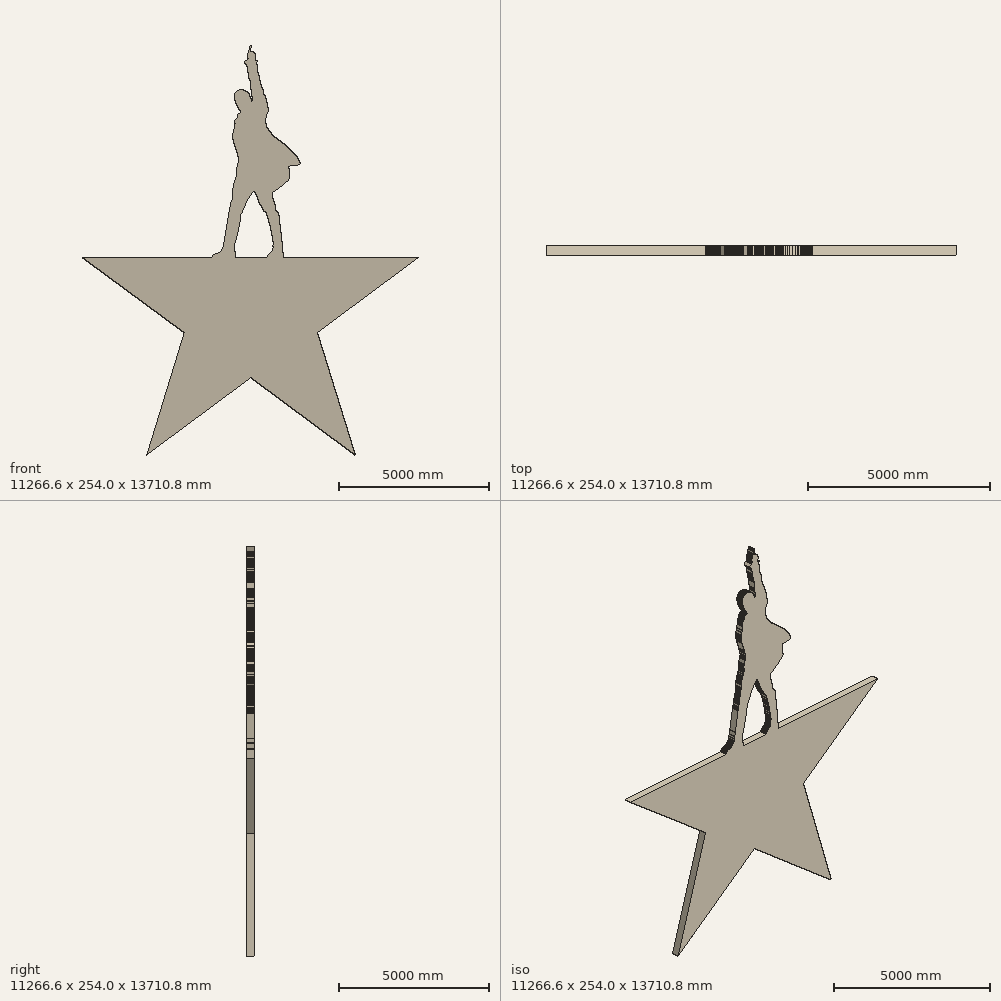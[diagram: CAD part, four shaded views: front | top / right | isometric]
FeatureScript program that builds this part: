
annotation { "Feature Type Name" : "Feature", "Feature Type Description" : "" }
export const myFeature = defineFeature(function(context is Context, id is Id, definition is map)
    precondition{}
    {
        {
            var Q0;
            Q0=qCreatedBy(makeId("Front.planeOp"),FACE);
            var sketch = newSketch(context, id + "F0", { "sketchPlane" : qUnion([Q0])});
            skLineSegment(sketch, "E0", {"start": v(-2213.01, -2754.08) * mm, "end": v(-3464.1, -6842.16) * mm});
            skLineSegment(sketch, "E1", {"start": v(-3464.1, -6842.16) * mm, "end": v(18.56, -4260.23) * mm});
            skLineSegment(sketch, "E2", {"start": v(18.56, -4260.23) * mm, "end": v(3513.04, -6855.37) * mm});
            skLineSegment(sketch, "E3", {"start": v(3513.04, -6855.37) * mm, "end": v(2240.88, -2755) * mm});
            skLineSegment(sketch, "E4", {"start": v(2240.88, -2755) * mm, "end": v(5633.28, -233.2) * mm});
            skLineSegment(sketch, "E5", {"start": v(5633.28, -233.2) * mm, "end": v(1116.7, -233.2) * mm});
            skLineSegment(sketch, "E6", {"start": v(1116.7, -233.2) * mm, "end": v(1111.2, -233.12) * mm});
            skLineSegment(sketch, "E7", {"start": v(1111.2, -233.12) * mm, "end": v(1117, -229) * mm});
            skLineSegment(sketch, "E8", {"start": v(1117, -229) * mm, "end": v(1065.8, 66.4) * mm});
            skLineSegment(sketch, "E9", {"start": v(1065.8, 66.4) * mm, "end": v(1064.67, 70.05) * mm});
            skLineSegment(sketch, "E10", {"start": v(1064.67, 70.05) * mm, "end": v(1064.67, 73.83) * mm});
            skLineSegment(sketch, "E11", {"start": v(1064.67, 73.83) * mm, "end": v(1064.87, 89.05) * mm});
            skLineSegment(sketch, "E12", {"start": v(1064.87, 89.05) * mm, "end": v(1057.1, 259.32) * mm});
            skLineSegment(sketch, "E13", {"start": v(1057.1, 259.32) * mm, "end": v(1054.52, 304.4) * mm});
            skLineSegment(sketch, "E14", {"start": v(1054.52, 304.4) * mm, "end": v(1051.17, 338.35) * mm});
            skLineSegment(sketch, "E15", {"start": v(1051.17, 338.35) * mm, "end": v(1041.6, 435.3) * mm});
            skLineSegment(sketch, "E16", {"start": v(1041.6, 435.3) * mm, "end": v(939.6, 1264.76) * mm});
            skLineSegment(sketch, "E17", {"start": v(939.6, 1264.76) * mm, "end": v(938.4, 1268.61) * mm});
            skLineSegment(sketch, "E18", {"start": v(938.4, 1268.61) * mm, "end": v(935.27, 1273.03) * mm});
            skLineSegment(sketch, "E19", {"start": v(935.27, 1273.03) * mm, "end": v(931.23, 1277.44) * mm});
            skLineSegment(sketch, "E20", {"start": v(931.23, 1277.44) * mm, "end": v(926.86, 1281.5) * mm});
            skLineSegment(sketch, "E21", {"start": v(926.86, 1281.5) * mm, "end": v(921.55, 1284.85) * mm});
            skLineSegment(sketch, "E22", {"start": v(921.55, 1284.85) * mm, "end": v(916.4, 1287.12) * mm});
            skLineSegment(sketch, "E23", {"start": v(916.4, 1287.12) * mm, "end": v(911.88, 1288.5) * mm});
            skLineSegment(sketch, "E24", {"start": v(911.88, 1288.5) * mm, "end": v(900.62, 1290.1) * mm});
            skLineSegment(sketch, "E25", {"start": v(900.62, 1290.1) * mm, "end": v(890.87, 1292.59) * mm});
            skLineSegment(sketch, "E26", {"start": v(890.87, 1292.59) * mm, "end": v(882.3, 1295.94) * mm});
            skLineSegment(sketch, "E27", {"start": v(882.3, 1295.94) * mm, "end": v(874.94, 1300.12) * mm});
            skLineSegment(sketch, "E28", {"start": v(874.94, 1300.12) * mm, "end": v(868.75, 1305.14) * mm});
            skLineSegment(sketch, "E29", {"start": v(868.75, 1305.14) * mm, "end": v(863.55, 1310.99) * mm});
            skLineSegment(sketch, "E30", {"start": v(863.55, 1310.99) * mm, "end": v(859.3, 1317.69) * mm});
            skLineSegment(sketch, "E31", {"start": v(859.3, 1317.69) * mm, "end": v(855.94, 1325.24) * mm});
            skLineSegment(sketch, "E32", {"start": v(855.94, 1325.24) * mm, "end": v(853.36, 1333.55) * mm});
            skLineSegment(sketch, "E33", {"start": v(853.36, 1333.55) * mm, "end": v(851.43, 1342.72) * mm});
            skLineSegment(sketch, "E34", {"start": v(851.43, 1342.72) * mm, "end": v(850.3, 1352.77) * mm});
            skLineSegment(sketch, "E35", {"start": v(850.3, 1352.77) * mm, "end": v(849.68, 1363.6) * mm});
            skLineSegment(sketch, "E36", {"start": v(849.68, 1363.6) * mm, "end": v(849.45, 1384.7) * mm});
            skLineSegment(sketch, "E37", {"start": v(849.45, 1384.7) * mm, "end": v(849.02, 1394.13) * mm});
            skLineSegment(sketch, "E38", {"start": v(849.02, 1394.13) * mm, "end": v(848.26, 1403.63) * mm});
            skLineSegment(sketch, "E39", {"start": v(848.26, 1403.63) * mm, "end": v(847.23, 1413.05) * mm});
            skLineSegment(sketch, "E40", {"start": v(847.23, 1413.05) * mm, "end": v(845.94, 1422.53) * mm});
            skLineSegment(sketch, "E41", {"start": v(845.94, 1422.53) * mm, "end": v(844.43, 1431.96) * mm});
            skLineSegment(sketch, "E42", {"start": v(844.43, 1431.96) * mm, "end": v(842.7, 1441.43) * mm});
            skLineSegment(sketch, "E43", {"start": v(842.7, 1441.43) * mm, "end": v(838.7, 1460.35) * mm});
            skLineSegment(sketch, "E44", {"start": v(838.7, 1460.35) * mm, "end": v(817.27, 1545) * mm});
            skLineSegment(sketch, "E45", {"start": v(817.27, 1545) * mm, "end": v(815.39, 1551.49) * mm});
            skLineSegment(sketch, "E46", {"start": v(815.39, 1551.49) * mm, "end": v(813.06, 1557.84) * mm});
            skLineSegment(sketch, "E47", {"start": v(813.06, 1557.84) * mm, "end": v(810.47, 1564.1) * mm});
            skLineSegment(sketch, "E48", {"start": v(810.47, 1564.1) * mm, "end": v(807.61, 1570.32) * mm});
            skLineSegment(sketch, "E49", {"start": v(807.61, 1570.32) * mm, "end": v(798.46, 1588.82) * mm});
            skLineSegment(sketch, "E50", {"start": v(798.46, 1588.82) * mm, "end": v(795.57, 1595.02) * mm});
            skLineSegment(sketch, "E51", {"start": v(795.57, 1595.02) * mm, "end": v(792.9, 1601.22) * mm});
            skLineSegment(sketch, "E52", {"start": v(792.9, 1601.22) * mm, "end": v(790.59, 1607.5) * mm});
            skLineSegment(sketch, "E53", {"start": v(790.59, 1607.5) * mm, "end": v(788.7, 1613.88) * mm});
            skLineSegment(sketch, "E54", {"start": v(788.7, 1613.88) * mm, "end": v(787.3, 1620.31) * mm});
            skLineSegment(sketch, "E55", {"start": v(787.3, 1620.31) * mm, "end": v(782.41, 1648.48) * mm});
            skLineSegment(sketch, "E56", {"start": v(782.41, 1648.48) * mm, "end": v(778.7, 1666.96) * mm});
            skLineSegment(sketch, "E57", {"start": v(778.7, 1666.96) * mm, "end": v(774.5, 1685.33) * mm});
            skLineSegment(sketch, "E58", {"start": v(774.5, 1685.33) * mm, "end": v(772.23, 1694.38) * mm});
            skLineSegment(sketch, "E59", {"start": v(772.23, 1694.38) * mm, "end": v(769.74, 1703.45) * mm});
            skLineSegment(sketch, "E60", {"start": v(769.74, 1703.45) * mm, "end": v(767.06, 1712.45) * mm});
            skLineSegment(sketch, "E61", {"start": v(767.06, 1712.45) * mm, "end": v(764.1, 1721.4) * mm});
            skLineSegment(sketch, "E62", {"start": v(764.1, 1721.4) * mm, "end": v(760.91, 1730.33) * mm});
            skLineSegment(sketch, "E63", {"start": v(760.91, 1730.33) * mm, "end": v(757.44, 1739.18) * mm});
            skLineSegment(sketch, "E64", {"start": v(757.44, 1739.18) * mm, "end": v(753.71, 1748.1) * mm});
            skLineSegment(sketch, "E65", {"start": v(753.71, 1748.1) * mm, "end": v(749.62, 1756.94) * mm});
            skLineSegment(sketch, "E66", {"start": v(749.62, 1756.94) * mm, "end": v(745.2, 1765.77) * mm});
            skLineSegment(sketch, "E67", {"start": v(745.2, 1765.77) * mm, "end": v(740.43, 1774.57) * mm});
            skLineSegment(sketch, "E68", {"start": v(740.43, 1774.57) * mm, "end": v(736.92, 1781.4) * mm});
            skLineSegment(sketch, "E69", {"start": v(736.92, 1781.4) * mm, "end": v(733.92, 1788.58) * mm});
            skLineSegment(sketch, "E70", {"start": v(733.92, 1788.58) * mm, "end": v(731.4, 1796.02) * mm});
            skLineSegment(sketch, "E71", {"start": v(731.4, 1796.02) * mm, "end": v(729.35, 1803.69) * mm});
            skLineSegment(sketch, "E72", {"start": v(729.35, 1803.69) * mm, "end": v(727.64, 1811.55) * mm});
            skLineSegment(sketch, "E73", {"start": v(727.64, 1811.55) * mm, "end": v(726.26, 1819.64) * mm});
            skLineSegment(sketch, "E74", {"start": v(726.26, 1819.64) * mm, "end": v(725.16, 1827.86) * mm});
            skLineSegment(sketch, "E75", {"start": v(725.16, 1827.86) * mm, "end": v(724.32, 1836.2) * mm});
            skLineSegment(sketch, "E76", {"start": v(724.32, 1836.2) * mm, "end": v(723.7, 1844.65) * mm});
            skLineSegment(sketch, "E77", {"start": v(723.7, 1844.65) * mm, "end": v(721.68, 1887.31) * mm});
            skLineSegment(sketch, "E78", {"start": v(721.68, 1887.31) * mm, "end": v(720.62, 1903.98) * mm});
            skLineSegment(sketch, "E79", {"start": v(720.62, 1903.98) * mm, "end": v(721.15, 1907.55) * mm});
            skLineSegment(sketch, "E80", {"start": v(721.15, 1907.55) * mm, "end": v(723.06, 1911.39) * mm});
            skLineSegment(sketch, "E81", {"start": v(723.06, 1911.39) * mm, "end": v(726.07, 1915.34) * mm});
            skLineSegment(sketch, "E82", {"start": v(726.07, 1915.34) * mm, "end": v(729.83, 1919.26) * mm});
            skLineSegment(sketch, "E83", {"start": v(729.83, 1919.26) * mm, "end": v(734.03, 1923) * mm});
            skLineSegment(sketch, "E84", {"start": v(734.03, 1923) * mm, "end": v(738.38, 1926.42) * mm});
            skLineSegment(sketch, "E85", {"start": v(738.38, 1926.42) * mm, "end": v(742.53, 1929.36) * mm});
            skLineSegment(sketch, "E86", {"start": v(742.53, 1929.36) * mm, "end": v(818.36, 1978.85) * mm});
            skLineSegment(sketch, "E87", {"start": v(818.36, 1978.85) * mm, "end": v(875.1, 2016.17) * mm});
            skLineSegment(sketch, "E88", {"start": v(875.1, 2016.17) * mm, "end": v(903, 2035.42) * mm});
            skLineSegment(sketch, "E89", {"start": v(903, 2035.42) * mm, "end": v(910.4, 2040.9) * mm});
            skLineSegment(sketch, "E90", {"start": v(910.4, 2040.9) * mm, "end": v(917.61, 2046.72) * mm});
            skLineSegment(sketch, "E91", {"start": v(917.61, 2046.72) * mm, "end": v(924.7, 2052.77) * mm});
            skLineSegment(sketch, "E92", {"start": v(924.7, 2052.77) * mm, "end": v(959.14, 2084.25) * mm});
            skLineSegment(sketch, "E93", {"start": v(959.14, 2084.25) * mm, "end": v(966.12, 2090.3) * mm});
            skLineSegment(sketch, "E94", {"start": v(966.12, 2090.3) * mm, "end": v(973.22, 2096.12) * mm});
            skLineSegment(sketch, "E95", {"start": v(973.22, 2096.12) * mm, "end": v(980.46, 2101.63) * mm});
            skLineSegment(sketch, "E96", {"start": v(980.46, 2101.63) * mm, "end": v(987.9, 2106.74) * mm});
            skLineSegment(sketch, "E97", {"start": v(987.9, 2106.74) * mm, "end": v(995.56, 2111.43) * mm});
            skLineSegment(sketch, "E98", {"start": v(995.56, 2111.43) * mm, "end": v(1017.24, 2122.53) * mm});
            skLineSegment(sketch, "E99", {"start": v(1017.24, 2122.53) * mm, "end": v(1030.63, 2130) * mm});
            skLineSegment(sketch, "E100", {"start": v(1030.63, 2130) * mm, "end": v(1043.62, 2137.91) * mm});
            skLineSegment(sketch, "E101", {"start": v(1043.62, 2137.91) * mm, "end": v(1056.26, 2146.22) * mm});
            skLineSegment(sketch, "E102", {"start": v(1056.26, 2146.22) * mm, "end": v(1068.54, 2154.93) * mm});
            skLineSegment(sketch, "E103", {"start": v(1068.54, 2154.93) * mm, "end": v(1080.56, 2163.94) * mm});
            skLineSegment(sketch, "E104", {"start": v(1080.56, 2163.94) * mm, "end": v(1092.31, 2173.26) * mm});
            skLineSegment(sketch, "E105", {"start": v(1092.31, 2173.26) * mm, "end": v(1103.82, 2182.85) * mm});
            skLineSegment(sketch, "E106", {"start": v(1103.82, 2182.85) * mm, "end": v(1126.3, 2202.66) * mm});
            skLineSegment(sketch, "E107", {"start": v(1126.3, 2202.66) * mm, "end": v(1202.34, 2274.96) * mm});
            skLineSegment(sketch, "E108", {"start": v(1202.34, 2274.96) * mm, "end": v(1224.34, 2295.26) * mm});
            skLineSegment(sketch, "E109", {"start": v(1224.34, 2295.26) * mm, "end": v(1255.09, 2321.92) * mm});
            skLineSegment(sketch, "E110", {"start": v(1255.09, 2321.92) * mm, "end": v(1262.74, 2329.19) * mm});
            skLineSegment(sketch, "E111", {"start": v(1262.74, 2329.19) * mm, "end": v(1269.9, 2336.66) * mm});
            skLineSegment(sketch, "E112", {"start": v(1269.9, 2336.66) * mm, "end": v(1276.58, 2344.37) * mm});
            skLineSegment(sketch, "E113", {"start": v(1276.58, 2344.37) * mm, "end": v(1282.73, 2352.3) * mm});
            skLineSegment(sketch, "E114", {"start": v(1282.73, 2352.3) * mm, "end": v(1288.32, 2360.47) * mm});
            skLineSegment(sketch, "E115", {"start": v(1288.32, 2360.47) * mm, "end": v(1293.36, 2368.9) * mm});
            skLineSegment(sketch, "E116", {"start": v(1293.36, 2368.9) * mm, "end": v(1297.81, 2377.58) * mm});
            skLineSegment(sketch, "E117", {"start": v(1297.81, 2377.58) * mm, "end": v(1301.66, 2386.5) * mm});
            skLineSegment(sketch, "E118", {"start": v(1301.66, 2386.5) * mm, "end": v(1304.88, 2395.7) * mm});
            skLineSegment(sketch, "E119", {"start": v(1304.88, 2395.7) * mm, "end": v(1307.45, 2405.18) * mm});
            skLineSegment(sketch, "E120", {"start": v(1307.45, 2405.18) * mm, "end": v(1309.37, 2414.94) * mm});
            skLineSegment(sketch, "E121", {"start": v(1309.37, 2414.94) * mm, "end": v(1310.6, 2425) * mm});
            skLineSegment(sketch, "E122", {"start": v(1310.6, 2425) * mm, "end": v(1311.13, 2435.34) * mm});
            skLineSegment(sketch, "E123", {"start": v(1311.13, 2435.34) * mm, "end": v(1310.94, 2445.99) * mm});
            skLineSegment(sketch, "E124", {"start": v(1310.94, 2445.99) * mm, "end": v(1310, 2456.93) * mm});
            skLineSegment(sketch, "E125", {"start": v(1310, 2456.93) * mm, "end": v(1308.3, 2468.22) * mm});
            skLineSegment(sketch, "E126", {"start": v(1308.3, 2468.22) * mm, "end": v(1307.11, 2475.3) * mm});
            skLineSegment(sketch, "E127", {"start": v(1307.11, 2475.3) * mm, "end": v(1306.1, 2482.4) * mm});
            skLineSegment(sketch, "E128", {"start": v(1306.1, 2482.4) * mm, "end": v(1305.21, 2489.53) * mm});
            skLineSegment(sketch, "E129", {"start": v(1305.21, 2489.53) * mm, "end": v(1303.86, 2503.87) * mm});
            skLineSegment(sketch, "E130", {"start": v(1303.86, 2503.87) * mm, "end": v(1299.82, 2572.18) * mm});
            skLineSegment(sketch, "E131", {"start": v(1299.82, 2572.18) * mm, "end": v(1296.68, 2668.61) * mm});
            skLineSegment(sketch, "E132", {"start": v(1296.68, 2668.61) * mm, "end": v(1295.55, 2689.96) * mm});
            skLineSegment(sketch, "E133", {"start": v(1295.55, 2689.96) * mm, "end": v(1293.87, 2711.15) * mm});
            skLineSegment(sketch, "E134", {"start": v(1293.87, 2711.15) * mm, "end": v(1292.76, 2721.68) * mm});
            skLineSegment(sketch, "E135", {"start": v(1292.76, 2721.68) * mm, "end": v(1291.43, 2732.15) * mm});
            skLineSegment(sketch, "E136", {"start": v(1291.43, 2732.15) * mm, "end": v(1289.87, 2742.56) * mm});
            skLineSegment(sketch, "E137", {"start": v(1289.87, 2742.56) * mm, "end": v(1288.05, 2752.9) * mm});
            skLineSegment(sketch, "E138", {"start": v(1288.05, 2752.9) * mm, "end": v(1285.94, 2763.17) * mm});
            skLineSegment(sketch, "E139", {"start": v(1285.94, 2763.17) * mm, "end": v(1281.15, 2783.65) * mm});
            skLineSegment(sketch, "E140", {"start": v(1281.15, 2783.65) * mm, "end": v(1279.68, 2792.43) * mm});
            skLineSegment(sketch, "E141", {"start": v(1279.68, 2792.43) * mm, "end": v(1279.04, 2799.8) * mm});
            skLineSegment(sketch, "E142", {"start": v(1279.04, 2799.8) * mm, "end": v(1279.25, 2805.94) * mm});
            skLineSegment(sketch, "E143", {"start": v(1279.25, 2805.94) * mm, "end": v(1280.3, 2810.94) * mm});
            skLineSegment(sketch, "E144", {"start": v(1280.3, 2810.94) * mm, "end": v(1282.19, 2814.92) * mm});
            skLineSegment(sketch, "E145", {"start": v(1282.19, 2814.92) * mm, "end": v(1284.86, 2818.02) * mm});
            skLineSegment(sketch, "E146", {"start": v(1284.86, 2818.02) * mm, "end": v(1288.31, 2820.36) * mm});
            skLineSegment(sketch, "E147", {"start": v(1288.31, 2820.36) * mm, "end": v(1292.53, 2822.09) * mm});
            skLineSegment(sketch, "E148", {"start": v(1292.53, 2822.09) * mm, "end": v(1297.5, 2823.32) * mm});
            skLineSegment(sketch, "E149", {"start": v(1297.5, 2823.32) * mm, "end": v(1303.18, 2824.17) * mm});
            skLineSegment(sketch, "E150", {"start": v(1303.18, 2824.17) * mm, "end": v(1309.6, 2824.77) * mm});
            skLineSegment(sketch, "E151", {"start": v(1309.6, 2824.77) * mm, "end": v(1337.24, 2826.57) * mm});
            skLineSegment(sketch, "E152", {"start": v(1337.24, 2826.57) * mm, "end": v(1401.12, 2829.48) * mm});
            skLineSegment(sketch, "E153", {"start": v(1401.12, 2829.48) * mm, "end": v(1452.21, 2832.06) * mm});
            skLineSegment(sketch, "E154", {"start": v(1452.21, 2832.06) * mm, "end": v(1477.7, 2833.98) * mm});
            skLineSegment(sketch, "E155", {"start": v(1477.7, 2833.98) * mm, "end": v(1503.08, 2836.6) * mm});
            skLineSegment(sketch, "E156", {"start": v(1503.08, 2836.6) * mm, "end": v(1515.72, 2838.24) * mm});
            skLineSegment(sketch, "E157", {"start": v(1515.72, 2838.24) * mm, "end": v(1528.34, 2840.14) * mm});
            skLineSegment(sketch, "E158", {"start": v(1528.34, 2840.14) * mm, "end": v(1540.9, 2842.3) * mm});
            skLineSegment(sketch, "E159", {"start": v(1540.9, 2842.3) * mm, "end": v(1553.45, 2844.78) * mm});
            skLineSegment(sketch, "E160", {"start": v(1553.45, 2844.78) * mm, "end": v(1565.93, 2847.57) * mm});
            skLineSegment(sketch, "E161", {"start": v(1565.93, 2847.57) * mm, "end": v(1578.39, 2850.72) * mm});
            skLineSegment(sketch, "E162", {"start": v(1578.39, 2850.72) * mm, "end": v(1590.77, 2854.25) * mm});
            skLineSegment(sketch, "E163", {"start": v(1590.77, 2854.25) * mm, "end": v(1603.1, 2858.19) * mm});
            skLineSegment(sketch, "E164", {"start": v(1603.1, 2858.19) * mm, "end": v(1615.38, 2862.55) * mm});
            skLineSegment(sketch, "E165", {"start": v(1615.38, 2862.55) * mm, "end": v(1642.78, 2873.49) * mm});
            skLineSegment(sketch, "E166", {"start": v(1642.78, 2873.49) * mm, "end": v(1647.78, 2875.72) * mm});
            skLineSegment(sketch, "E167", {"start": v(1647.78, 2875.72) * mm, "end": v(1652.5, 2878.13) * mm});
            skLineSegment(sketch, "E168", {"start": v(1652.5, 2878.13) * mm, "end": v(1656.8, 2880.81) * mm});
            skLineSegment(sketch, "E169", {"start": v(1656.8, 2880.81) * mm, "end": v(1660.57, 2883.79) * mm});
            skLineSegment(sketch, "E170", {"start": v(1660.57, 2883.79) * mm, "end": v(1663.64, 2887.13) * mm});
            skLineSegment(sketch, "E171", {"start": v(1663.64, 2887.13) * mm, "end": v(1665.89, 2890.9) * mm});
            skLineSegment(sketch, "E172", {"start": v(1665.89, 2890.9) * mm, "end": v(1667.17, 2895.16) * mm});
            skLineSegment(sketch, "E173", {"start": v(1667.17, 2895.16) * mm, "end": v(1667.34, 2899.94) * mm});
            skLineSegment(sketch, "E174", {"start": v(1667.34, 2899.94) * mm, "end": v(1666.27, 2905.33) * mm});
            skLineSegment(sketch, "E175", {"start": v(1666.27, 2905.33) * mm, "end": v(1663.82, 2911.38) * mm});
            skLineSegment(sketch, "E176", {"start": v(1663.82, 2911.38) * mm, "end": v(1657.73, 2923.67) * mm});
            skLineSegment(sketch, "E177", {"start": v(1657.73, 2923.67) * mm, "end": v(1622.19, 2998.44) * mm});
            skLineSegment(sketch, "E178", {"start": v(1622.19, 2998.44) * mm, "end": v(1598.2, 3048.23) * mm});
            skLineSegment(sketch, "E179", {"start": v(1598.2, 3048.23) * mm, "end": v(1585.68, 3072.77) * mm});
            skLineSegment(sketch, "E180", {"start": v(1585.68, 3072.77) * mm, "end": v(1572.79, 3096.85) * mm});
            skLineSegment(sketch, "E181", {"start": v(1572.79, 3096.85) * mm, "end": v(1559.06, 3120.55) * mm});
            skLineSegment(sketch, "E182", {"start": v(1559.06, 3120.55) * mm, "end": v(1551.97, 3132.16) * mm});
            skLineSegment(sketch, "E183", {"start": v(1551.97, 3132.16) * mm, "end": v(1544.66, 3143.58) * mm});
            skLineSegment(sketch, "E184", {"start": v(1544.66, 3143.58) * mm, "end": v(1537.14, 3154.82) * mm});
            skLineSegment(sketch, "E185", {"start": v(1537.14, 3154.82) * mm, "end": v(1529.37, 3165.87) * mm});
            skLineSegment(sketch, "E186", {"start": v(1529.37, 3165.87) * mm, "end": v(1521.34, 3176.7) * mm});
            skLineSegment(sketch, "E187", {"start": v(1521.34, 3176.7) * mm, "end": v(1513.04, 3187.32) * mm});
            skLineSegment(sketch, "E188", {"start": v(1513.04, 3187.32) * mm, "end": v(1487.25, 3218.58) * mm});
            skLineSegment(sketch, "E189", {"start": v(1487.25, 3218.58) * mm, "end": v(1460.72, 3249.2) * mm});
            skLineSegment(sketch, "E190", {"start": v(1460.72, 3249.2) * mm, "end": v(1433.53, 3279.2) * mm});
            skLineSegment(sketch, "E191", {"start": v(1433.53, 3279.2) * mm, "end": v(1405.7, 3308.61) * mm});
            skLineSegment(sketch, "E192", {"start": v(1405.7, 3308.61) * mm, "end": v(1377.29, 3337.48) * mm});
            skLineSegment(sketch, "E193", {"start": v(1377.29, 3337.48) * mm, "end": v(1348.34, 3365.84) * mm});
            skLineSegment(sketch, "E194", {"start": v(1348.34, 3365.84) * mm, "end": v(1303.99, 3407.47) * mm});
            skLineSegment(sketch, "E195", {"start": v(1303.99, 3407.47) * mm, "end": v(1258.67, 3448.16) * mm});
            skLineSegment(sketch, "E196", {"start": v(1258.67, 3448.16) * mm, "end": v(1197, 3501.1) * mm});
            skLineSegment(sketch, "E197", {"start": v(1197, 3501.1) * mm, "end": v(1134.25, 3552.8) * mm});
            skLineSegment(sketch, "E198", {"start": v(1134.25, 3552.8) * mm, "end": v(1038.09, 3629.16) * mm});
            skLineSegment(sketch, "E199", {"start": v(1038.09, 3629.16) * mm, "end": v(983.62, 3670.65) * mm});
            skLineSegment(sketch, "E200", {"start": v(983.62, 3670.65) * mm, "end": v(939.4, 3702.89) * mm});
            skLineSegment(sketch, "E201", {"start": v(939.4, 3702.89) * mm, "end": v(868.45, 3751.5) * mm});
            skLineSegment(sketch, "E202", {"start": v(868.45, 3751.5) * mm, "end": v(854.3, 3761.78) * mm});
            skLineSegment(sketch, "E203", {"start": v(854.3, 3761.78) * mm, "end": v(840.48, 3772.4) * mm});
            skLineSegment(sketch, "E204", {"start": v(840.48, 3772.4) * mm, "end": v(827.01, 3783.34) * mm});
            skLineSegment(sketch, "E205", {"start": v(827.01, 3783.34) * mm, "end": v(813.87, 3794.56) * mm});
            skLineSegment(sketch, "E206", {"start": v(813.87, 3794.56) * mm, "end": v(801.06, 3806.07) * mm});
            skLineSegment(sketch, "E207", {"start": v(801.06, 3806.07) * mm, "end": v(788.52, 3817.87) * mm});
            skLineSegment(sketch, "E208", {"start": v(788.52, 3817.87) * mm, "end": v(776.26, 3829.92) * mm});
            skLineSegment(sketch, "E209", {"start": v(776.26, 3829.92) * mm, "end": v(764.25, 3842.19) * mm});
            skLineSegment(sketch, "E210", {"start": v(764.25, 3842.19) * mm, "end": v(752.5, 3854.66) * mm});
            skLineSegment(sketch, "E211", {"start": v(752.5, 3854.66) * mm, "end": v(729.62, 3880.2) * mm});
            skLineSegment(sketch, "E212", {"start": v(729.62, 3880.2) * mm, "end": v(707.5, 3906.4) * mm});
            skLineSegment(sketch, "E213", {"start": v(707.5, 3906.4) * mm, "end": v(685.98, 3933.1) * mm});
            skLineSegment(sketch, "E214", {"start": v(685.98, 3933.1) * mm, "end": v(654.54, 3973.76) * mm});
            skLineSegment(sketch, "E215", {"start": v(654.54, 3973.76) * mm, "end": v(596.44, 4051.32) * mm});
            skLineSegment(sketch, "E216", {"start": v(596.44, 4051.32) * mm, "end": v(589.87, 4060.78) * mm});
            skLineSegment(sketch, "E217", {"start": v(589.87, 4060.78) * mm, "end": v(583.48, 4070.5) * mm});
            skLineSegment(sketch, "E218", {"start": v(583.48, 4070.5) * mm, "end": v(577.28, 4080.44) * mm});
            skLineSegment(sketch, "E219", {"start": v(577.28, 4080.44) * mm, "end": v(571.27, 4090.64) * mm});
            skLineSegment(sketch, "E220", {"start": v(571.27, 4090.64) * mm, "end": v(565.5, 4101.02) * mm});
            skLineSegment(sketch, "E221", {"start": v(565.5, 4101.02) * mm, "end": v(559.93, 4111.59) * mm});
            skLineSegment(sketch, "E222", {"start": v(559.93, 4111.59) * mm, "end": v(554.64, 4122.3) * mm});
            skLineSegment(sketch, "E223", {"start": v(554.64, 4122.3) * mm, "end": v(549.6, 4133.15) * mm});
            skLineSegment(sketch, "E224", {"start": v(549.6, 4133.15) * mm, "end": v(544.83, 4144.15) * mm});
            skLineSegment(sketch, "E225", {"start": v(544.83, 4144.15) * mm, "end": v(540.35, 4155.24) * mm});
            skLineSegment(sketch, "E226", {"start": v(540.35, 4155.24) * mm, "end": v(536.18, 4166.4) * mm});
            skLineSegment(sketch, "E227", {"start": v(536.18, 4166.4) * mm, "end": v(532.33, 4177.65) * mm});
            skLineSegment(sketch, "E228", {"start": v(532.33, 4177.65) * mm, "end": v(528.8, 4188.92) * mm});
            skLineSegment(sketch, "E229", {"start": v(528.8, 4188.92) * mm, "end": v(525.66, 4200.21) * mm});
            skLineSegment(sketch, "E230", {"start": v(525.66, 4200.21) * mm, "end": v(522.84, 4211.57) * mm});
            skLineSegment(sketch, "E231", {"start": v(522.84, 4211.57) * mm, "end": v(520.4, 4222.85) * mm});
            skLineSegment(sketch, "E232", {"start": v(520.4, 4222.85) * mm, "end": v(518.36, 4234.15) * mm});
            skLineSegment(sketch, "E233", {"start": v(518.36, 4234.15) * mm, "end": v(516.7, 4245.37) * mm});
            skLineSegment(sketch, "E234", {"start": v(516.7, 4245.37) * mm, "end": v(515.48, 4256.53) * mm});
            skLineSegment(sketch, "E235", {"start": v(515.48, 4256.53) * mm, "end": v(514.4, 4269.27) * mm});
            skLineSegment(sketch, "E236", {"start": v(514.4, 4269.27) * mm, "end": v(512.82, 4294.9) * mm});
            skLineSegment(sketch, "E237", {"start": v(512.82, 4294.9) * mm, "end": v(512.08, 4320.68) * mm});
            skLineSegment(sketch, "E238", {"start": v(512.08, 4320.68) * mm, "end": v(512.05, 4333.6) * mm});
            skLineSegment(sketch, "E239", {"start": v(512.05, 4333.6) * mm, "end": v(512.27, 4346.54) * mm});
            skLineSegment(sketch, "E240", {"start": v(512.27, 4346.54) * mm, "end": v(512.74, 4359.49) * mm});
            skLineSegment(sketch, "E241", {"start": v(512.74, 4359.49) * mm, "end": v(513.49, 4372.47) * mm});
            skLineSegment(sketch, "E242", {"start": v(513.49, 4372.47) * mm, "end": v(514.5, 4385.38) * mm});
            skLineSegment(sketch, "E243", {"start": v(514.5, 4385.38) * mm, "end": v(515.8, 4398.32) * mm});
            skLineSegment(sketch, "E244", {"start": v(515.8, 4398.32) * mm, "end": v(517.44, 4411.2) * mm});
            skLineSegment(sketch, "E245", {"start": v(517.44, 4411.2) * mm, "end": v(519.37, 4424.07) * mm});
            skLineSegment(sketch, "E246", {"start": v(519.37, 4424.07) * mm, "end": v(521.6, 4436.8) * mm});
            skLineSegment(sketch, "E247", {"start": v(521.6, 4436.8) * mm, "end": v(524.26, 4449.61) * mm});
            skLineSegment(sketch, "E248", {"start": v(524.26, 4449.61) * mm, "end": v(527.2, 4462.31) * mm});
            skLineSegment(sketch, "E249", {"start": v(527.2, 4462.31) * mm, "end": v(530.53, 4474.94) * mm});
            skLineSegment(sketch, "E250", {"start": v(530.53, 4474.94) * mm, "end": v(534.24, 4487.49) * mm});
            skLineSegment(sketch, "E251", {"start": v(534.24, 4487.49) * mm, "end": v(538.33, 4499.94) * mm});
            skLineSegment(sketch, "E252", {"start": v(538.33, 4499.94) * mm, "end": v(542.84, 4512.3) * mm});
            skLineSegment(sketch, "E253", {"start": v(542.84, 4512.3) * mm, "end": v(547.76, 4524.6) * mm});
            skLineSegment(sketch, "E254", {"start": v(547.76, 4524.6) * mm, "end": v(553.1, 4536.74) * mm});
            skLineSegment(sketch, "E255", {"start": v(553.1, 4536.74) * mm, "end": v(558.89, 4548.77) * mm});
            skLineSegment(sketch, "E256", {"start": v(558.89, 4548.77) * mm, "end": v(570.64, 4571.36) * mm});
            skLineSegment(sketch, "E257", {"start": v(570.64, 4571.36) * mm, "end": v(575.66, 4582.05) * mm});
            skLineSegment(sketch, "E258", {"start": v(575.66, 4582.05) * mm, "end": v(580.11, 4592.74) * mm});
            skLineSegment(sketch, "E259", {"start": v(580.11, 4592.74) * mm, "end": v(584.04, 4603.47) * mm});
            skLineSegment(sketch, "E260", {"start": v(584.04, 4603.47) * mm, "end": v(587.45, 4614.2) * mm});
            skLineSegment(sketch, "E261", {"start": v(587.45, 4614.2) * mm, "end": v(590.37, 4624.98) * mm});
            skLineSegment(sketch, "E262", {"start": v(590.37, 4624.98) * mm, "end": v(592.81, 4635.76) * mm});
            skLineSegment(sketch, "E263", {"start": v(592.81, 4635.76) * mm, "end": v(594.77, 4646.58) * mm});
            skLineSegment(sketch, "E264", {"start": v(594.77, 4646.58) * mm, "end": v(596.27, 4657.43) * mm});
            skLineSegment(sketch, "E265", {"start": v(596.27, 4657.43) * mm, "end": v(597.34, 4668.31) * mm});
            skLineSegment(sketch, "E266", {"start": v(597.34, 4668.31) * mm, "end": v(597.98, 4679.22) * mm});
            skLineSegment(sketch, "E267", {"start": v(597.98, 4679.22) * mm, "end": v(598.2, 4690.18) * mm});
            skLineSegment(sketch, "E268", {"start": v(598.2, 4690.18) * mm, "end": v(598.05, 4701.18) * mm});
            skLineSegment(sketch, "E269", {"start": v(598.05, 4701.18) * mm, "end": v(597.5, 4712.22) * mm});
            skLineSegment(sketch, "E270", {"start": v(597.5, 4712.22) * mm, "end": v(596.58, 4723.33) * mm});
            skLineSegment(sketch, "E271", {"start": v(596.58, 4723.33) * mm, "end": v(595.3, 4734.45) * mm});
            skLineSegment(sketch, "E272", {"start": v(595.3, 4734.45) * mm, "end": v(593.68, 4745.65) * mm});
            skLineSegment(sketch, "E273", {"start": v(593.68, 4745.65) * mm, "end": v(591.75, 4756.91) * mm});
            skLineSegment(sketch, "E274", {"start": v(591.75, 4756.91) * mm, "end": v(589.5, 4768.23) * mm});
            skLineSegment(sketch, "E275", {"start": v(589.5, 4768.23) * mm, "end": v(581.91, 4801.45) * mm});
            skLineSegment(sketch, "E276", {"start": v(581.91, 4801.45) * mm, "end": v(549.99, 4955.17) * mm});
            skLineSegment(sketch, "E277", {"start": v(549.99, 4955.17) * mm, "end": v(538.02, 5009.96) * mm});
            skLineSegment(sketch, "E278", {"start": v(538.02, 5009.96) * mm, "end": v(534.01, 5026.56) * mm});
            skLineSegment(sketch, "E279", {"start": v(534.01, 5026.56) * mm, "end": v(527.44, 5051.34) * mm});
            skLineSegment(sketch, "E280", {"start": v(527.44, 5051.34) * mm, "end": v(500.62, 5141.56) * mm});
            skLineSegment(sketch, "E281", {"start": v(500.62, 5141.56) * mm, "end": v(497.7, 5150.02) * mm});
            skLineSegment(sketch, "E282", {"start": v(497.7, 5150.02) * mm, "end": v(494.13, 5158.23) * mm});
            skLineSegment(sketch, "E283", {"start": v(494.13, 5158.23) * mm, "end": v(490.03, 5166.17) * mm});
            skLineSegment(sketch, "E284", {"start": v(490.03, 5166.17) * mm, "end": v(485.52, 5173.95) * mm});
            skLineSegment(sketch, "E285", {"start": v(485.52, 5173.95) * mm, "end": v(480.71, 5181.58) * mm});
            skLineSegment(sketch, "E286", {"start": v(480.71, 5181.58) * mm, "end": v(465.74, 5204.26) * mm});
            skLineSegment(sketch, "E287", {"start": v(465.74, 5204.26) * mm, "end": v(460.96, 5211.93) * mm});
            skLineSegment(sketch, "E288", {"start": v(460.96, 5211.93) * mm, "end": v(456.47, 5219.72) * mm});
            skLineSegment(sketch, "E289", {"start": v(456.47, 5219.72) * mm, "end": v(452.4, 5227.7) * mm});
            skLineSegment(sketch, "E290", {"start": v(452.4, 5227.7) * mm, "end": v(448.88, 5235.92) * mm});
            skLineSegment(sketch, "E291", {"start": v(448.88, 5235.92) * mm, "end": v(446, 5244.45) * mm});
            skLineSegment(sketch, "E292", {"start": v(446, 5244.45) * mm, "end": v(443.9, 5253.32) * mm});
            skLineSegment(sketch, "E293", {"start": v(443.9, 5253.32) * mm, "end": v(442.69, 5262.6) * mm});
            skLineSegment(sketch, "E294", {"start": v(442.69, 5262.6) * mm, "end": v(442.49, 5272.31) * mm});
            skLineSegment(sketch, "E295", {"start": v(442.49, 5272.31) * mm, "end": v(442.75, 5281.64) * mm});
            skLineSegment(sketch, "E296", {"start": v(442.75, 5281.64) * mm, "end": v(442.84, 5290.9) * mm});
            skLineSegment(sketch, "E297", {"start": v(442.84, 5290.9) * mm, "end": v(442.71, 5300.1) * mm});
            skLineSegment(sketch, "E298", {"start": v(442.71, 5300.1) * mm, "end": v(442.33, 5309.19) * mm});
            skLineSegment(sketch, "E299", {"start": v(442.33, 5309.19) * mm, "end": v(441.6, 5318.17) * mm});
            skLineSegment(sketch, "E300", {"start": v(441.6, 5318.17) * mm, "end": v(440.5, 5327.03) * mm});
            skLineSegment(sketch, "E301", {"start": v(440.5, 5327.03) * mm, "end": v(438.98, 5335.75) * mm});
            skLineSegment(sketch, "E302", {"start": v(438.98, 5335.75) * mm, "end": v(436.98, 5344.3) * mm});
            skLineSegment(sketch, "E303", {"start": v(436.98, 5344.3) * mm, "end": v(434.43, 5352.7) * mm});
            skLineSegment(sketch, "E304", {"start": v(434.43, 5352.7) * mm, "end": v(431.3, 5360.89) * mm});
            skLineSegment(sketch, "E305", {"start": v(431.3, 5360.89) * mm, "end": v(427.52, 5368.88) * mm});
            skLineSegment(sketch, "E306", {"start": v(427.52, 5368.88) * mm, "end": v(423.04, 5376.65) * mm});
            skLineSegment(sketch, "E307", {"start": v(423.04, 5376.65) * mm, "end": v(417.81, 5384.2) * mm});
            skLineSegment(sketch, "E308", {"start": v(417.81, 5384.2) * mm, "end": v(411.79, 5391.46) * mm});
            skLineSegment(sketch, "E309", {"start": v(411.79, 5391.46) * mm, "end": v(404.9, 5398.48) * mm});
            skLineSegment(sketch, "E310", {"start": v(404.9, 5398.48) * mm, "end": v(397.1, 5405.2) * mm});
            skLineSegment(sketch, "E311", {"start": v(397.1, 5405.2) * mm, "end": v(394.5, 5407.91) * mm});
            skLineSegment(sketch, "E312", {"start": v(394.5, 5407.91) * mm, "end": v(392.45, 5411.33) * mm});
            skLineSegment(sketch, "E313", {"start": v(392.45, 5411.33) * mm, "end": v(390.82, 5415.28) * mm});
            skLineSegment(sketch, "E314", {"start": v(390.82, 5415.28) * mm, "end": v(389.5, 5419.63) * mm});
            skLineSegment(sketch, "E315", {"start": v(389.5, 5419.63) * mm, "end": v(386.3, 5433.46) * mm});
            skLineSegment(sketch, "E316", {"start": v(386.3, 5433.46) * mm, "end": v(385.1, 5437.83) * mm});
            skLineSegment(sketch, "E317", {"start": v(385.1, 5437.83) * mm, "end": v(320.17, 5646.94) * mm});
            skLineSegment(sketch, "E318", {"start": v(320.17, 5646.94) * mm, "end": v(319.4, 5650.34) * mm});
            skLineSegment(sketch, "E319", {"start": v(319.4, 5650.34) * mm, "end": v(319.05, 5653.85) * mm});
            skLineSegment(sketch, "E320", {"start": v(319.05, 5653.85) * mm, "end": v(318.96, 5657.44) * mm});
            skLineSegment(sketch, "E321", {"start": v(318.96, 5657.44) * mm, "end": v(319.03, 5664.73) * mm});
            skLineSegment(sketch, "E322", {"start": v(319.03, 5664.73) * mm, "end": v(318.93, 5668.35) * mm});
            skLineSegment(sketch, "E323", {"start": v(318.93, 5668.35) * mm, "end": v(318.53, 5671.91) * mm});
            skLineSegment(sketch, "E324", {"start": v(318.53, 5671.91) * mm, "end": v(316.72, 5682.24) * mm});
            skLineSegment(sketch, "E325", {"start": v(316.72, 5682.24) * mm, "end": v(308.25, 5724.9) * mm});
            skLineSegment(sketch, "E326", {"start": v(308.25, 5724.9) * mm, "end": v(309.64, 5728.19) * mm});
            skLineSegment(sketch, "E327", {"start": v(309.64, 5728.19) * mm, "end": v(313.72, 5736.4) * mm});
            skLineSegment(sketch, "E328", {"start": v(313.72, 5736.4) * mm, "end": v(315.73, 5740.98) * mm});
            skLineSegment(sketch, "E329", {"start": v(315.73, 5740.98) * mm, "end": v(317.27, 5745.67) * mm});
            skLineSegment(sketch, "E330", {"start": v(317.27, 5745.67) * mm, "end": v(318, 5750.3) * mm});
            skLineSegment(sketch, "E331", {"start": v(318, 5750.3) * mm, "end": v(317.57, 5754.7) * mm});
            skLineSegment(sketch, "E332", {"start": v(317.57, 5754.7) * mm, "end": v(315.6, 5761.94) * mm});
            skLineSegment(sketch, "E333", {"start": v(315.6, 5761.94) * mm, "end": v(311.26, 5776.31) * mm});
            skLineSegment(sketch, "E334", {"start": v(311.26, 5776.31) * mm, "end": v(306.5, 5790.58) * mm});
            skLineSegment(sketch, "E335", {"start": v(306.5, 5790.58) * mm, "end": v(301.43, 5804.77) * mm});
            skLineSegment(sketch, "E336", {"start": v(301.43, 5804.77) * mm, "end": v(282.84, 5854.06) * mm});
            skLineSegment(sketch, "E337", {"start": v(282.84, 5854.06) * mm, "end": v(267.66, 5888.48) * mm});
            skLineSegment(sketch, "E338", {"start": v(267.66, 5888.48) * mm, "end": v(264.77, 5895.37) * mm});
            skLineSegment(sketch, "E339", {"start": v(264.77, 5895.37) * mm, "end": v(262.08, 5902.28) * mm});
            skLineSegment(sketch, "E340", {"start": v(262.08, 5902.28) * mm, "end": v(259.68, 5909.24) * mm});
            skLineSegment(sketch, "E341", {"start": v(259.68, 5909.24) * mm, "end": v(257.62, 5916.23) * mm});
            skLineSegment(sketch, "E342", {"start": v(257.62, 5916.23) * mm, "end": v(255.98, 5923.28) * mm});
            skLineSegment(sketch, "E343", {"start": v(255.98, 5923.28) * mm, "end": v(254.82, 5930.4) * mm});
            skLineSegment(sketch, "E344", {"start": v(254.82, 5930.4) * mm, "end": v(253.44, 5941.58) * mm});
            skLineSegment(sketch, "E345", {"start": v(253.44, 5941.58) * mm, "end": v(248.53, 5986.38) * mm});
            skLineSegment(sketch, "E346", {"start": v(248.53, 5986.38) * mm, "end": v(244.44, 6031.29) * mm});
            skLineSegment(sketch, "E347", {"start": v(244.44, 6031.29) * mm, "end": v(240.34, 6087.53) * mm});
            skLineSegment(sketch, "E348", {"start": v(240.34, 6087.53) * mm, "end": v(236.66, 6155.05) * mm});
            skLineSegment(sketch, "E349", {"start": v(236.66, 6155.05) * mm, "end": v(236.06, 6163.93) * mm});
            skLineSegment(sketch, "E350", {"start": v(236.06, 6163.93) * mm, "end": v(235.04, 6172.34) * mm});
            skLineSegment(sketch, "E351", {"start": v(235.04, 6172.34) * mm, "end": v(233.48, 6180.25) * mm});
            skLineSegment(sketch, "E352", {"start": v(233.48, 6180.25) * mm, "end": v(231.29, 6187.62) * mm});
            skLineSegment(sketch, "E353", {"start": v(231.29, 6187.62) * mm, "end": v(228.35, 6194.44) * mm});
            skLineSegment(sketch, "E354", {"start": v(228.35, 6194.44) * mm, "end": v(224.55, 6200.64) * mm});
            skLineSegment(sketch, "E355", {"start": v(224.55, 6200.64) * mm, "end": v(219.78, 6206.2) * mm});
            skLineSegment(sketch, "E356", {"start": v(219.78, 6206.2) * mm, "end": v(213.94, 6211.1) * mm});
            skLineSegment(sketch, "E357", {"start": v(213.94, 6211.1) * mm, "end": v(206.92, 6215.28) * mm});
            skLineSegment(sketch, "E358", {"start": v(206.92, 6215.28) * mm, "end": v(198.61, 6218.71) * mm});
            skLineSegment(sketch, "E359", {"start": v(198.61, 6218.71) * mm, "end": v(188.9, 6221.37) * mm});
            skLineSegment(sketch, "E360", {"start": v(188.9, 6221.37) * mm, "end": v(177.7, 6223.22) * mm});
            skLineSegment(sketch, "E361", {"start": v(177.7, 6223.22) * mm, "end": v(201.1, 6267.3) * mm});
            skLineSegment(sketch, "E362", {"start": v(201.1, 6267.3) * mm, "end": v(207.4, 6278.31) * mm});
            skLineSegment(sketch, "E363", {"start": v(207.4, 6278.31) * mm, "end": v(210.64, 6283.64) * mm});
            skLineSegment(sketch, "E364", {"start": v(210.64, 6283.64) * mm, "end": v(214, 6288.85) * mm});
            skLineSegment(sketch, "E365", {"start": v(214, 6288.85) * mm, "end": v(217.43, 6293.78) * mm});
            skLineSegment(sketch, "E366", {"start": v(217.43, 6293.78) * mm, "end": v(221.09, 6298.57) * mm});
            skLineSegment(sketch, "E367", {"start": v(221.09, 6298.57) * mm, "end": v(224.92, 6303.24) * mm});
            skLineSegment(sketch, "E368", {"start": v(224.92, 6303.24) * mm, "end": v(228.88, 6307.82) * mm});
            skLineSegment(sketch, "E369", {"start": v(228.88, 6307.82) * mm, "end": v(241.17, 6321.3) * mm});
            skLineSegment(sketch, "E370", {"start": v(241.17, 6321.3) * mm, "end": v(249.26, 6330.35) * mm});
            skLineSegment(sketch, "E371", {"start": v(249.26, 6330.35) * mm, "end": v(244.05, 6332.1) * mm});
            skLineSegment(sketch, "E372", {"start": v(244.05, 6332.1) * mm, "end": v(223.2, 6340) * mm});
            skLineSegment(sketch, "E373", {"start": v(223.2, 6340) * mm, "end": v(217.98, 6341.8) * mm});
            skLineSegment(sketch, "E374", {"start": v(217.98, 6341.8) * mm, "end": v(212.76, 6343.38) * mm});
            skLineSegment(sketch, "E375", {"start": v(212.76, 6343.38) * mm, "end": v(207.52, 6344.65) * mm});
            skLineSegment(sketch, "E376", {"start": v(207.52, 6344.65) * mm, "end": v(202.28, 6345.55) * mm});
            skLineSegment(sketch, "E377", {"start": v(202.28, 6345.55) * mm, "end": v(186, 6346.85) * mm});
            skLineSegment(sketch, "E378", {"start": v(186, 6346.85) * mm, "end": v(176.53, 6348.68) * mm});
            skLineSegment(sketch, "E379", {"start": v(176.53, 6348.68) * mm, "end": v(168.61, 6351.5) * mm});
            skLineSegment(sketch, "E380", {"start": v(168.61, 6351.5) * mm, "end": v(162.25, 6355.34) * mm});
            skLineSegment(sketch, "E381", {"start": v(162.25, 6355.34) * mm, "end": v(157.43, 6360.25) * mm});
            skLineSegment(sketch, "E382", {"start": v(157.43, 6360.25) * mm, "end": v(154.15, 6366.26) * mm});
            skLineSegment(sketch, "E383", {"start": v(154.15, 6366.26) * mm, "end": v(152.41, 6373.4) * mm});
            skLineSegment(sketch, "E384", {"start": v(152.41, 6373.4) * mm, "end": v(152.2, 6381.72) * mm});
            skLineSegment(sketch, "E385", {"start": v(152.2, 6381.72) * mm, "end": v(153.54, 6391.24) * mm});
            skLineSegment(sketch, "E386", {"start": v(153.54, 6391.24) * mm, "end": v(156.39, 6402) * mm});
            skLineSegment(sketch, "E387", {"start": v(156.39, 6402) * mm, "end": v(158.48, 6408.2) * mm});
            skLineSegment(sketch, "E388", {"start": v(158.48, 6408.2) * mm, "end": v(167.82, 6433.3) * mm});
            skLineSegment(sketch, "E389", {"start": v(167.82, 6433.3) * mm, "end": v(169.91, 6439.6) * mm});
            skLineSegment(sketch, "E390", {"start": v(169.91, 6439.6) * mm, "end": v(171.72, 6445.84) * mm});
            skLineSegment(sketch, "E391", {"start": v(171.72, 6445.84) * mm, "end": v(173.13, 6452.06) * mm});
            skLineSegment(sketch, "E392", {"start": v(173.13, 6452.06) * mm, "end": v(174.05, 6458.2) * mm});
            skLineSegment(sketch, "E393", {"start": v(174.05, 6458.2) * mm, "end": v(174.38, 6464.27) * mm});
            skLineSegment(sketch, "E394", {"start": v(174.38, 6464.27) * mm, "end": v(174.03, 6470.25) * mm});
            skLineSegment(sketch, "E395", {"start": v(174.03, 6470.25) * mm, "end": v(169.95, 6507.28) * mm});
            skLineSegment(sketch, "E396", {"start": v(169.95, 6507.28) * mm, "end": v(167.5, 6526.2) * mm});
            skLineSegment(sketch, "E397", {"start": v(167.5, 6526.2) * mm, "end": v(166, 6535.52) * mm});
            skLineSegment(sketch, "E398", {"start": v(166, 6535.52) * mm, "end": v(164.24, 6544.68) * mm});
            skLineSegment(sketch, "E399", {"start": v(164.24, 6544.68) * mm, "end": v(162.17, 6553.6) * mm});
            skLineSegment(sketch, "E400", {"start": v(162.17, 6553.6) * mm, "end": v(159.74, 6562.23) * mm});
            skLineSegment(sketch, "E401", {"start": v(159.74, 6562.23) * mm, "end": v(156.9, 6570.49) * mm});
            skLineSegment(sketch, "E402", {"start": v(156.9, 6570.49) * mm, "end": v(153.6, 6578.31) * mm});
            skLineSegment(sketch, "E403", {"start": v(153.6, 6578.31) * mm, "end": v(149.77, 6585.64) * mm});
            skLineSegment(sketch, "E404", {"start": v(149.77, 6585.64) * mm, "end": v(145.4, 6592.42) * mm});
            skLineSegment(sketch, "E405", {"start": v(145.4, 6592.42) * mm, "end": v(140.4, 6598.57) * mm});
            skLineSegment(sketch, "E406", {"start": v(140.4, 6598.57) * mm, "end": v(133.8, 6605.23) * mm});
            skLineSegment(sketch, "E407", {"start": v(133.8, 6605.23) * mm, "end": v(126.72, 6611.43) * mm});
            skLineSegment(sketch, "E408", {"start": v(126.72, 6611.43) * mm, "end": v(119.18, 6617.24) * mm});
            skLineSegment(sketch, "E409", {"start": v(119.18, 6617.24) * mm, "end": v(111.23, 6622.67) * mm});
            skLineSegment(sketch, "E410", {"start": v(111.23, 6622.67) * mm, "end": v(102.92, 6627.8) * mm});
            skLineSegment(sketch, "E411", {"start": v(102.92, 6627.8) * mm, "end": v(94.3, 6632.64) * mm});
            skLineSegment(sketch, "E412", {"start": v(94.3, 6632.64) * mm, "end": v(85.4, 6637.27) * mm});
            skLineSegment(sketch, "E413", {"start": v(85.4, 6637.27) * mm, "end": v(76.28, 6641.71) * mm});
            skLineSegment(sketch, "E414", {"start": v(76.28, 6641.71) * mm, "end": v(28.98, 6662.9) * mm});
            skLineSegment(sketch, "E415", {"start": v(28.98, 6662.9) * mm, "end": v(10.13, 6671.75) * mm});
            skLineSegment(sketch, "E416", {"start": v(10.13, 6671.75) * mm, "end": v(0.9, 6676.45) * mm});
            skLineSegment(sketch, "E417", {"start": v(0.9, 6676.45) * mm, "end": v(36.67, 6855.25) * mm});
            skLineSegment(sketch, "E418", {"start": v(36.67, 6855.25) * mm, "end": v(26.67, 6855.43) * mm});
            skLineSegment(sketch, "E419", {"start": v(26.67, 6855.43) * mm, "end": v(18.07, 6854.3) * mm});
            skLineSegment(sketch, "E420", {"start": v(18.07, 6854.3) * mm, "end": v(10.73, 6852) * mm});
            skLineSegment(sketch, "E421", {"start": v(10.73, 6852) * mm, "end": v(4.53, 6848.64) * mm});
            skLineSegment(sketch, "E422", {"start": v(4.53, 6848.64) * mm, "end": v(-0.68, 6844.4) * mm});
            skLineSegment(sketch, "E423", {"start": v(-0.68, 6844.4) * mm, "end": v(-5.01, 6839.4) * mm});
            skLineSegment(sketch, "E424", {"start": v(-5.01, 6839.4) * mm, "end": v(-8.61, 6833.79) * mm});
            skLineSegment(sketch, "E425", {"start": v(-8.61, 6833.79) * mm, "end": v(-11.62, 6827.7) * mm});
            skLineSegment(sketch, "E426", {"start": v(-11.62, 6827.7) * mm, "end": v(-14.16, 6821.27) * mm});
            skLineSegment(sketch, "E427", {"start": v(-14.16, 6821.27) * mm, "end": v(-16.37, 6814.64) * mm});
            skLineSegment(sketch, "E428", {"start": v(-16.37, 6814.64) * mm, "end": v(-18.39, 6807.96) * mm});
            skLineSegment(sketch, "E429", {"start": v(-18.39, 6807.96) * mm, "end": v(-24.6, 6786.2) * mm});
            skLineSegment(sketch, "E430", {"start": v(-24.6, 6786.2) * mm, "end": v(-44.85, 6709.5) * mm});
            skLineSegment(sketch, "E431", {"start": v(-44.85, 6709.5) * mm, "end": v(-56.77, 6665.83) * mm});
            skLineSegment(sketch, "E432", {"start": v(-56.77, 6665.83) * mm, "end": v(-63.2, 6644.18) * mm});
            skLineSegment(sketch, "E433", {"start": v(-63.2, 6644.18) * mm, "end": v(-70.07, 6622.72) * mm});
            skLineSegment(sketch, "E434", {"start": v(-70.07, 6622.72) * mm, "end": v(-77.56, 6601.46) * mm});
            skLineSegment(sketch, "E435", {"start": v(-77.56, 6601.46) * mm, "end": v(-85.44, 6580.9) * mm});
            skLineSegment(sketch, "E436", {"start": v(-85.44, 6580.9) * mm, "end": v(-92.83, 6561.09) * mm});
            skLineSegment(sketch, "E437", {"start": v(-92.83, 6561.09) * mm, "end": v(-96.19, 6551.32) * mm});
            skLineSegment(sketch, "E438", {"start": v(-96.19, 6551.32) * mm, "end": v(-99.26, 6541.6) * mm});
            skLineSegment(sketch, "E439", {"start": v(-99.26, 6541.6) * mm, "end": v(-101.96, 6531.92) * mm});
            skLineSegment(sketch, "E440", {"start": v(-101.96, 6531.92) * mm, "end": v(-104.23, 6522.3) * mm});
            skLineSegment(sketch, "E441", {"start": v(-104.23, 6522.3) * mm, "end": v(-106, 6512.7) * mm});
            skLineSegment(sketch, "E442", {"start": v(-106, 6512.7) * mm, "end": v(-107.22, 6503.14) * mm});
            skLineSegment(sketch, "E443", {"start": v(-107.22, 6503.14) * mm, "end": v(-107.8, 6493.56) * mm});
            skLineSegment(sketch, "E444", {"start": v(-107.8, 6493.56) * mm, "end": v(-107.71, 6484) * mm});
            skLineSegment(sketch, "E445", {"start": v(-107.71, 6484) * mm, "end": v(-106.86, 6474.42) * mm});
            skLineSegment(sketch, "E446", {"start": v(-106.86, 6474.42) * mm, "end": v(-105.2, 6464.84) * mm});
            skLineSegment(sketch, "E447", {"start": v(-105.2, 6464.84) * mm, "end": v(-102.65, 6455.2) * mm});
            skLineSegment(sketch, "E448", {"start": v(-102.65, 6455.2) * mm, "end": v(-99.16, 6445.54) * mm});
            skLineSegment(sketch, "E449", {"start": v(-99.16, 6445.54) * mm, "end": v(-94.66, 6435.82) * mm});
            skLineSegment(sketch, "E450", {"start": v(-94.66, 6435.82) * mm, "end": v(-89.08, 6426.04) * mm});
            skLineSegment(sketch, "E451", {"start": v(-89.08, 6426.04) * mm, "end": v(-82.37, 6416.19) * mm});
            skLineSegment(sketch, "E452", {"start": v(-82.37, 6416.19) * mm, "end": v(-81.38, 6413.55) * mm});
            skLineSegment(sketch, "E453", {"start": v(-81.38, 6413.55) * mm, "end": v(-81.3, 6409.85) * mm});
            skLineSegment(sketch, "E454", {"start": v(-81.3, 6409.85) * mm, "end": v(-81.98, 6405.45) * mm});
            skLineSegment(sketch, "E455", {"start": v(-81.98, 6405.45) * mm, "end": v(-83.33, 6400.68) * mm});
            skLineSegment(sketch, "E456", {"start": v(-83.33, 6400.68) * mm, "end": v(-85.22, 6395.88) * mm});
            skLineSegment(sketch, "E457", {"start": v(-85.22, 6395.88) * mm, "end": v(-87.53, 6391.4) * mm});
            skLineSegment(sketch, "E458", {"start": v(-87.53, 6391.4) * mm, "end": v(-90.15, 6387.59) * mm});
            skLineSegment(sketch, "E459", {"start": v(-90.15, 6387.59) * mm, "end": v(-92.95, 6384.77) * mm});
            skLineSegment(sketch, "E460", {"start": v(-92.95, 6384.77) * mm, "end": v(-117, 6366.52) * mm});
            skLineSegment(sketch, "E461", {"start": v(-117, 6366.52) * mm, "end": v(-224.43, 6289.21) * mm});
            skLineSegment(sketch, "E462", {"start": v(-224.43, 6289.21) * mm, "end": v(-175.06, 6235.16) * mm});
            skLineSegment(sketch, "E463", {"start": v(-175.06, 6235.16) * mm, "end": v(-120.98, 6174.9) * mm});
            skLineSegment(sketch, "E464", {"start": v(-120.98, 6174.9) * mm, "end": v(-118.3, 6171.53) * mm});
            skLineSegment(sketch, "E465", {"start": v(-118.3, 6171.53) * mm, "end": v(-115.84, 6167.84) * mm});
            skLineSegment(sketch, "E466", {"start": v(-115.84, 6167.84) * mm, "end": v(-113.65, 6163.88) * mm});
            skLineSegment(sketch, "E467", {"start": v(-113.65, 6163.88) * mm, "end": v(-111.78, 6159.74) * mm});
            skLineSegment(sketch, "E468", {"start": v(-111.78, 6159.74) * mm, "end": v(-110.29, 6155.5) * mm});
            skLineSegment(sketch, "E469", {"start": v(-110.29, 6155.5) * mm, "end": v(-109.22, 6151.24) * mm});
            skLineSegment(sketch, "E470", {"start": v(-109.22, 6151.24) * mm, "end": v(-108.64, 6147.05) * mm});
            skLineSegment(sketch, "E471", {"start": v(-108.64, 6147.05) * mm, "end": v(-106.13, 6111.8) * mm});
            skLineSegment(sketch, "E472", {"start": v(-106.13, 6111.8) * mm, "end": v(-100.57, 6005.96) * mm});
            skLineSegment(sketch, "E473", {"start": v(-100.57, 6005.96) * mm, "end": v(-100.87, 6002.35) * mm});
            skLineSegment(sketch, "E474", {"start": v(-100.87, 6002.35) * mm, "end": v(-101.82, 5998.59) * mm});
            skLineSegment(sketch, "E475", {"start": v(-101.82, 5998.59) * mm, "end": v(-103, 5994.83) * mm});
            skLineSegment(sketch, "E476", {"start": v(-103, 5994.83) * mm, "end": v(-103.99, 5991.24) * mm});
            skLineSegment(sketch, "E477", {"start": v(-103.99, 5991.24) * mm, "end": v(-104.36, 5987.98) * mm});
            skLineSegment(sketch, "E478", {"start": v(-104.36, 5987.98) * mm, "end": v(-103.7, 5985.22) * mm});
            skLineSegment(sketch, "E479", {"start": v(-103.7, 5985.22) * mm, "end": v(-98.57, 5975.2) * mm});
            skLineSegment(sketch, "E480", {"start": v(-98.57, 5975.2) * mm, "end": v(-93.8, 5965.09) * mm});
            skLineSegment(sketch, "E481", {"start": v(-93.8, 5965.09) * mm, "end": v(-89.37, 5954.9) * mm});
            skLineSegment(sketch, "E482", {"start": v(-89.37, 5954.9) * mm, "end": v(-85.28, 5944.65) * mm});
            skLineSegment(sketch, "E483", {"start": v(-85.28, 5944.65) * mm, "end": v(-81.5, 5934.33) * mm});
            skLineSegment(sketch, "E484", {"start": v(-81.5, 5934.33) * mm, "end": v(-78.02, 5923.94) * mm});
            skLineSegment(sketch, "E485", {"start": v(-78.02, 5923.94) * mm, "end": v(-74.83, 5913.47) * mm});
            skLineSegment(sketch, "E486", {"start": v(-74.83, 5913.47) * mm, "end": v(-71.91, 5902.96) * mm});
            skLineSegment(sketch, "E487", {"start": v(-71.91, 5902.96) * mm, "end": v(-69.25, 5892.37) * mm});
            skLineSegment(sketch, "E488", {"start": v(-69.25, 5892.37) * mm, "end": v(-66.84, 5881.73) * mm});
            skLineSegment(sketch, "E489", {"start": v(-66.84, 5881.73) * mm, "end": v(-64.65, 5871.04) * mm});
            skLineSegment(sketch, "E490", {"start": v(-64.65, 5871.04) * mm, "end": v(-62.68, 5860.3) * mm});
            skLineSegment(sketch, "E491", {"start": v(-62.68, 5860.3) * mm, "end": v(-60.91, 5849.49) * mm});
            skLineSegment(sketch, "E492", {"start": v(-60.91, 5849.49) * mm, "end": v(-59.33, 5838.64) * mm});
            skLineSegment(sketch, "E493", {"start": v(-59.33, 5838.64) * mm, "end": v(-56.68, 5816.8) * mm});
            skLineSegment(sketch, "E494", {"start": v(-56.68, 5816.8) * mm, "end": v(-54.6, 5794.8) * mm});
            skLineSegment(sketch, "E495", {"start": v(-54.6, 5794.8) * mm, "end": v(-52.97, 5772.66) * mm});
            skLineSegment(sketch, "E496", {"start": v(-52.97, 5772.66) * mm, "end": v(-52.24, 5766.94) * mm});
            skLineSegment(sketch, "E497", {"start": v(-52.24, 5766.94) * mm, "end": v(-50.86, 5761.27) * mm});
            skLineSegment(sketch, "E498", {"start": v(-50.86, 5761.27) * mm, "end": v(-48.96, 5755.63) * mm});
            skLineSegment(sketch, "E499", {"start": v(-48.96, 5755.63) * mm, "end": v(-46.63, 5750.02) * mm});
            skLineSegment(sketch, "E500", {"start": v(-46.63, 5750.02) * mm, "end": v(-44.01, 5744.43) * mm});
            skLineSegment(sketch, "E501", {"start": v(-44.01, 5744.43) * mm, "end": v(-35.48, 5727.66) * mm});
            skLineSegment(sketch, "E502", {"start": v(-35.48, 5727.66) * mm, "end": v(-32.79, 5722.05) * mm});
            skLineSegment(sketch, "E503", {"start": v(-32.79, 5722.05) * mm, "end": v(-27.77, 5710.08) * mm});
            skLineSegment(sketch, "E504", {"start": v(-27.77, 5710.08) * mm, "end": v(-13.61, 5678.53) * mm});
            skLineSegment(sketch, "E505", {"start": v(-13.61, 5678.53) * mm, "end": v(-10.99, 5672.2) * mm});
            skLineSegment(sketch, "E506", {"start": v(-10.99, 5672.2) * mm, "end": v(-8.58, 5665.83) * mm});
            skLineSegment(sketch, "E507", {"start": v(-8.58, 5665.83) * mm, "end": v(-6.45, 5659.43) * mm});
            skLineSegment(sketch, "E508", {"start": v(-6.45, 5659.43) * mm, "end": v(-4.66, 5653) * mm});
            skLineSegment(sketch, "E509", {"start": v(-4.66, 5653) * mm, "end": v(-3.28, 5646.54) * mm});
            skLineSegment(sketch, "E510", {"start": v(-3.28, 5646.54) * mm, "end": v(-2.36, 5640.03) * mm});
            skLineSegment(sketch, "E511", {"start": v(-2.36, 5640.03) * mm, "end": v(15.66, 5404.6) * mm});
            skLineSegment(sketch, "E512", {"start": v(15.66, 5404.6) * mm, "end": v(20.45, 5355.16) * mm});
            skLineSegment(sketch, "E513", {"start": v(20.45, 5355.16) * mm, "end": v(25.01, 5317.52) * mm});
            skLineSegment(sketch, "E514", {"start": v(25.01, 5317.52) * mm, "end": v(30.42, 5279.66) * mm});
            skLineSegment(sketch, "E515", {"start": v(30.42, 5279.66) * mm, "end": v(51.18, 5153.76) * mm});
            skLineSegment(sketch, "E516", {"start": v(51.18, 5153.76) * mm, "end": v(61.08, 5090.74) * mm});
            skLineSegment(sketch, "E517", {"start": v(61.08, 5090.74) * mm, "end": v(66.21, 5052.83) * mm});
            skLineSegment(sketch, "E518", {"start": v(66.21, 5052.83) * mm, "end": v(66.9, 5045.85) * mm});
            skLineSegment(sketch, "E519", {"start": v(66.9, 5045.85) * mm, "end": v(67.25, 5038.82) * mm});
            skLineSegment(sketch, "E520", {"start": v(67.25, 5038.82) * mm, "end": v(67.3, 5031.7) * mm});
            skLineSegment(sketch, "E521", {"start": v(67.3, 5031.7) * mm, "end": v(67.1, 5024.5) * mm});
            skLineSegment(sketch, "E522", {"start": v(67.1, 5024.5) * mm, "end": v(66.66, 5017.2) * mm});
            skLineSegment(sketch, "E523", {"start": v(66.66, 5017.2) * mm, "end": v(66.03, 5009.78) * mm});
            skLineSegment(sketch, "E524", {"start": v(66.03, 5009.78) * mm, "end": v(58.92, 4953.4) * mm});
            skLineSegment(sketch, "E525", {"start": v(58.92, 4953.4) * mm, "end": v(57.04, 4935.43) * mm});
            skLineSegment(sketch, "E526", {"start": v(57.04, 4935.43) * mm, "end": v(54.84, 4945.87) * mm});
            skLineSegment(sketch, "E527", {"start": v(54.84, 4945.87) * mm, "end": v(52.93, 4956.18) * mm});
            skLineSegment(sketch, "E528", {"start": v(52.93, 4956.18) * mm, "end": v(51.25, 4966.34) * mm});
            skLineSegment(sketch, "E529", {"start": v(51.25, 4966.34) * mm, "end": v(46.98, 4995.66) * mm});
            skLineSegment(sketch, "E530", {"start": v(46.98, 4995.66) * mm, "end": v(44.17, 5013.97) * mm});
            skLineSegment(sketch, "E531", {"start": v(44.17, 5013.97) * mm, "end": v(42.58, 5022.7) * mm});
            skLineSegment(sketch, "E532", {"start": v(42.58, 5022.7) * mm, "end": v(40.8, 5031.07) * mm});
            skLineSegment(sketch, "E533", {"start": v(40.8, 5031.07) * mm, "end": v(38.76, 5039.1) * mm});
            skLineSegment(sketch, "E534", {"start": v(38.76, 5039.1) * mm, "end": v(36.4, 5046.74) * mm});
            skLineSegment(sketch, "E535", {"start": v(36.4, 5046.74) * mm, "end": v(33.66, 5053.98) * mm});
            skLineSegment(sketch, "E536", {"start": v(33.66, 5053.98) * mm, "end": v(30.48, 5060.78) * mm});
            skLineSegment(sketch, "E537", {"start": v(30.48, 5060.78) * mm, "end": v(26.79, 5067.12) * mm});
            skLineSegment(sketch, "E538", {"start": v(26.79, 5067.12) * mm, "end": v(22.53, 5072.99) * mm});
            skLineSegment(sketch, "E539", {"start": v(22.53, 5072.99) * mm, "end": v(16.5, 5081) * mm});
            skLineSegment(sketch, "E540", {"start": v(16.5, 5081) * mm, "end": v(11.17, 5089.2) * mm});
            skLineSegment(sketch, "E541", {"start": v(11.17, 5089.2) * mm, "end": v(6.49, 5097.52) * mm});
            skLineSegment(sketch, "E542", {"start": v(6.49, 5097.52) * mm, "end": v(2.35, 5105.96) * mm});
            skLineSegment(sketch, "E543", {"start": v(2.35, 5105.96) * mm, "end": v(-1.32, 5114.5) * mm});
            skLineSegment(sketch, "E544", {"start": v(-1.32, 5114.5) * mm, "end": v(-4.62, 5123.1) * mm});
            skLineSegment(sketch, "E545", {"start": v(-4.62, 5123.1) * mm, "end": v(-7.64, 5131.77) * mm});
            skLineSegment(sketch, "E546", {"start": v(-7.64, 5131.77) * mm, "end": v(-18.59, 5166.5) * mm});
            skLineSegment(sketch, "E547", {"start": v(-18.59, 5166.5) * mm, "end": v(-21.5, 5175.08) * mm});
            skLineSegment(sketch, "E548", {"start": v(-21.5, 5175.08) * mm, "end": v(-24.64, 5183.59) * mm});
            skLineSegment(sketch, "E549", {"start": v(-24.64, 5183.59) * mm, "end": v(-28.1, 5192) * mm});
            skLineSegment(sketch, "E550", {"start": v(-28.1, 5192) * mm, "end": v(-32, 5200.26) * mm});
            skLineSegment(sketch, "E551", {"start": v(-32, 5200.26) * mm, "end": v(-34.3, 5205.78) * mm});
            skLineSegment(sketch, "E552", {"start": v(-34.3, 5205.78) * mm, "end": v(-36.03, 5211.77) * mm});
            skLineSegment(sketch, "E553", {"start": v(-36.03, 5211.77) * mm, "end": v(-37.34, 5218.1) * mm});
            skLineSegment(sketch, "E554", {"start": v(-37.34, 5218.1) * mm, "end": v(-40.24, 5237.48) * mm});
            skLineSegment(sketch, "E555", {"start": v(-40.24, 5237.48) * mm, "end": v(-41.37, 5243.57) * mm});
            skLineSegment(sketch, "E556", {"start": v(-41.37, 5243.57) * mm, "end": v(-42.81, 5249.22) * mm});
            skLineSegment(sketch, "E557", {"start": v(-42.81, 5249.22) * mm, "end": v(-44.73, 5254.28) * mm});
            skLineSegment(sketch, "E558", {"start": v(-44.73, 5254.28) * mm, "end": v(-47.27, 5258.6) * mm});
            skLineSegment(sketch, "E559", {"start": v(-47.27, 5258.6) * mm, "end": v(-50.59, 5262.01) * mm});
            skLineSegment(sketch, "E560", {"start": v(-50.59, 5262.01) * mm, "end": v(-67.47, 5274.97) * mm});
            skLineSegment(sketch, "E561", {"start": v(-67.47, 5274.97) * mm, "end": v(-93.27, 5293.96) * mm});
            skLineSegment(sketch, "E562", {"start": v(-93.27, 5293.96) * mm, "end": v(-110.78, 5306.24) * mm});
            skLineSegment(sketch, "E563", {"start": v(-110.78, 5306.24) * mm, "end": v(-128.55, 5318.13) * mm});
            skLineSegment(sketch, "E564", {"start": v(-128.55, 5318.13) * mm, "end": v(-146.58, 5329.58) * mm});
            skLineSegment(sketch, "E565", {"start": v(-146.58, 5329.58) * mm, "end": v(-164.88, 5340.53) * mm});
            skLineSegment(sketch, "E566", {"start": v(-164.88, 5340.53) * mm, "end": v(-183.45, 5350.92) * mm});
            skLineSegment(sketch, "E567", {"start": v(-183.45, 5350.92) * mm, "end": v(-202.3, 5360.69) * mm});
            skLineSegment(sketch, "E568", {"start": v(-202.3, 5360.69) * mm, "end": v(-211.28, 5364.8) * mm});
            skLineSegment(sketch, "E569", {"start": v(-211.28, 5364.8) * mm, "end": v(-220.34, 5368.27) * mm});
            skLineSegment(sketch, "E570", {"start": v(-220.34, 5368.27) * mm, "end": v(-229.46, 5371.11) * mm});
            skLineSegment(sketch, "E571", {"start": v(-229.46, 5371.11) * mm, "end": v(-238.66, 5373.38) * mm});
            skLineSegment(sketch, "E572", {"start": v(-238.66, 5373.38) * mm, "end": v(-247.9, 5375.09) * mm});
            skLineSegment(sketch, "E573", {"start": v(-247.9, 5375.09) * mm, "end": v(-257.2, 5376.28) * mm});
            skLineSegment(sketch, "E574", {"start": v(-257.2, 5376.28) * mm, "end": v(-266.56, 5376.99) * mm});
            skLineSegment(sketch, "E575", {"start": v(-266.56, 5376.99) * mm, "end": v(-275.96, 5377.26) * mm});
            skLineSegment(sketch, "E576", {"start": v(-275.96, 5377.26) * mm, "end": v(-285.41, 5377.1) * mm});
            skLineSegment(sketch, "E577", {"start": v(-285.41, 5377.1) * mm, "end": v(-294.9, 5376.57) * mm});
            skLineSegment(sketch, "E578", {"start": v(-294.9, 5376.57) * mm, "end": v(-304.43, 5375.68) * mm});
            skLineSegment(sketch, "E579", {"start": v(-304.43, 5375.68) * mm, "end": v(-313.99, 5374.48) * mm});
            skLineSegment(sketch, "E580", {"start": v(-313.99, 5374.48) * mm, "end": v(-323.58, 5373) * mm});
            skLineSegment(sketch, "E581", {"start": v(-323.58, 5373) * mm, "end": v(-333.2, 5371.28) * mm});
            skLineSegment(sketch, "E582", {"start": v(-333.2, 5371.28) * mm, "end": v(-342.84, 5369.34) * mm});
            skLineSegment(sketch, "E583", {"start": v(-342.84, 5369.34) * mm, "end": v(-352.5, 5367.2) * mm});
            skLineSegment(sketch, "E584", {"start": v(-352.5, 5367.2) * mm, "end": v(-371.88, 5362.56) * mm});
            skLineSegment(sketch, "E585", {"start": v(-371.88, 5362.56) * mm, "end": v(-385.62, 5358.52) * mm});
            skLineSegment(sketch, "E586", {"start": v(-385.62, 5358.52) * mm, "end": v(-399.16, 5353.38) * mm});
            skLineSegment(sketch, "E587", {"start": v(-399.16, 5353.38) * mm, "end": v(-412.42, 5347.2) * mm});
            skLineSegment(sketch, "E588", {"start": v(-412.42, 5347.2) * mm, "end": v(-425.34, 5340.03) * mm});
            skLineSegment(sketch, "E589", {"start": v(-425.34, 5340.03) * mm, "end": v(-437.88, 5331.94) * mm});
            skLineSegment(sketch, "E590", {"start": v(-437.88, 5331.94) * mm, "end": v(-449.96, 5323) * mm});
            skLineSegment(sketch, "E591", {"start": v(-449.96, 5323) * mm, "end": v(-461.52, 5313.3) * mm});
            skLineSegment(sketch, "E592", {"start": v(-461.52, 5313.3) * mm, "end": v(-472.52, 5302.85) * mm});
            skLineSegment(sketch, "E593", {"start": v(-472.52, 5302.85) * mm, "end": v(-482.88, 5291.75) * mm});
            skLineSegment(sketch, "E594", {"start": v(-482.88, 5291.75) * mm, "end": v(-492.55, 5280.06) * mm});
            skLineSegment(sketch, "E595", {"start": v(-492.55, 5280.06) * mm, "end": v(-501.47, 5267.82) * mm});
            skLineSegment(sketch, "E596", {"start": v(-501.47, 5267.82) * mm, "end": v(-509.58, 5255.13) * mm});
            skLineSegment(sketch, "E597", {"start": v(-509.58, 5255.13) * mm, "end": v(-516.82, 5242.02) * mm});
            skLineSegment(sketch, "E598", {"start": v(-516.82, 5242.02) * mm, "end": v(-523.14, 5228.6) * mm});
            skLineSegment(sketch, "E599", {"start": v(-523.14, 5228.6) * mm, "end": v(-528.46, 5214.87) * mm});
            skLineSegment(sketch, "E600", {"start": v(-528.46, 5214.87) * mm, "end": v(-532.73, 5200.94) * mm});
            skLineSegment(sketch, "E601", {"start": v(-532.73, 5200.94) * mm, "end": v(-535.9, 5186.86) * mm});
            skLineSegment(sketch, "E602", {"start": v(-535.9, 5186.86) * mm, "end": v(-537.9, 5172.7) * mm});
            skLineSegment(sketch, "E603", {"start": v(-537.9, 5172.7) * mm, "end": v(-538.66, 5158.52) * mm});
            skLineSegment(sketch, "E604", {"start": v(-538.66, 5158.52) * mm, "end": v(-538.56, 5142.44) * mm});
            skLineSegment(sketch, "E605", {"start": v(-538.56, 5142.44) * mm, "end": v(-537.93, 5126.55) * mm});
            skLineSegment(sketch, "E606", {"start": v(-537.93, 5126.55) * mm, "end": v(-536.8, 5110.79) * mm});
            skLineSegment(sketch, "E607", {"start": v(-536.8, 5110.79) * mm, "end": v(-535.2, 5095.2) * mm});
            skLineSegment(sketch, "E608", {"start": v(-535.2, 5095.2) * mm, "end": v(-533.14, 5079.75) * mm});
            skLineSegment(sketch, "E609", {"start": v(-533.14, 5079.75) * mm, "end": v(-530.64, 5064.44) * mm});
            skLineSegment(sketch, "E610", {"start": v(-530.64, 5064.44) * mm, "end": v(-527.74, 5049.27) * mm});
            skLineSegment(sketch, "E611", {"start": v(-527.74, 5049.27) * mm, "end": v(-524.43, 5034.23) * mm});
            skLineSegment(sketch, "E612", {"start": v(-524.43, 5034.23) * mm, "end": v(-520.76, 5019.3) * mm});
            skLineSegment(sketch, "E613", {"start": v(-520.76, 5019.3) * mm, "end": v(-516.72, 5004.5) * mm});
            skLineSegment(sketch, "E614", {"start": v(-516.72, 5004.5) * mm, "end": v(-512.36, 4989.8) * mm});
            skLineSegment(sketch, "E615", {"start": v(-512.36, 4989.8) * mm, "end": v(-507.68, 4975.2) * mm});
            skLineSegment(sketch, "E616", {"start": v(-507.68, 4975.2) * mm, "end": v(-502.72, 4960.68) * mm});
            skLineSegment(sketch, "E617", {"start": v(-502.72, 4960.68) * mm, "end": v(-492, 4931.93) * mm});
            skLineSegment(sketch, "E618", {"start": v(-492, 4931.93) * mm, "end": v(-480.36, 4903.44) * mm});
            skLineSegment(sketch, "E619", {"start": v(-480.36, 4903.44) * mm, "end": v(-467.96, 4875.22) * mm});
            skLineSegment(sketch, "E620", {"start": v(-467.96, 4875.22) * mm, "end": v(-454.99, 4847.17) * mm});
            skLineSegment(sketch, "E621", {"start": v(-454.99, 4847.17) * mm, "end": v(-414.19, 4763.6) * mm});
            skLineSegment(sketch, "E622", {"start": v(-414.19, 4763.6) * mm, "end": v(-409.16, 4754.05) * mm});
            skLineSegment(sketch, "E623", {"start": v(-409.16, 4754.05) * mm, "end": v(-403.66, 4744.7) * mm});
            skLineSegment(sketch, "E624", {"start": v(-403.66, 4744.7) * mm, "end": v(-397.8, 4735.54) * mm});
            skLineSegment(sketch, "E625", {"start": v(-397.8, 4735.54) * mm, "end": v(-391.68, 4726.5) * mm});
            skLineSegment(sketch, "E626", {"start": v(-391.68, 4726.5) * mm, "end": v(-366.2, 4690.76) * mm});
            skLineSegment(sketch, "E627", {"start": v(-366.2, 4690.76) * mm, "end": v(-360.02, 4681.7) * mm});
            skLineSegment(sketch, "E628", {"start": v(-360.02, 4681.7) * mm, "end": v(-354.11, 4672.5) * mm});
            skLineSegment(sketch, "E629", {"start": v(-354.11, 4672.5) * mm, "end": v(-348.56, 4663.11) * mm});
            skLineSegment(sketch, "E630", {"start": v(-348.56, 4663.11) * mm, "end": v(-343.44, 4653.5) * mm});
            skLineSegment(sketch, "E631", {"start": v(-343.44, 4653.5) * mm, "end": v(-338.85, 4643.6) * mm});
            skLineSegment(sketch, "E632", {"start": v(-338.85, 4643.6) * mm, "end": v(-334.88, 4633.4) * mm});
            skLineSegment(sketch, "E633", {"start": v(-334.88, 4633.4) * mm, "end": v(-331.62, 4622.83) * mm});
            skLineSegment(sketch, "E634", {"start": v(-331.62, 4622.83) * mm, "end": v(-329.15, 4611.85) * mm});
            skLineSegment(sketch, "E635", {"start": v(-329.15, 4611.85) * mm, "end": v(-327.57, 4600.42) * mm});
            skLineSegment(sketch, "E636", {"start": v(-327.57, 4600.42) * mm, "end": v(-326.97, 4588.48) * mm});
            skLineSegment(sketch, "E637", {"start": v(-326.97, 4588.48) * mm, "end": v(-338.38, 4588.93) * mm});
            skLineSegment(sketch, "E638", {"start": v(-338.38, 4588.93) * mm, "end": v(-349.76, 4588.26) * mm});
            skLineSegment(sketch, "E639", {"start": v(-349.76, 4588.26) * mm, "end": v(-360.98, 4586.48) * mm});
            skLineSegment(sketch, "E640", {"start": v(-360.98, 4586.48) * mm, "end": v(-371.93, 4583.61) * mm});
            skLineSegment(sketch, "E641", {"start": v(-371.93, 4583.61) * mm, "end": v(-382.51, 4579.7) * mm});
            skLineSegment(sketch, "E642", {"start": v(-382.51, 4579.7) * mm, "end": v(-392.63, 4574.74) * mm});
            skLineSegment(sketch, "E643", {"start": v(-392.63, 4574.74) * mm, "end": v(-402.17, 4568.8) * mm});
            skLineSegment(sketch, "E644", {"start": v(-402.17, 4568.8) * mm, "end": v(-411.03, 4561.86) * mm});
            skLineSegment(sketch, "E645", {"start": v(-411.03, 4561.86) * mm, "end": v(-419.11, 4553.98) * mm});
            skLineSegment(sketch, "E646", {"start": v(-419.11, 4553.98) * mm, "end": v(-426.31, 4545.18) * mm});
            skLineSegment(sketch, "E647", {"start": v(-426.31, 4545.18) * mm, "end": v(-432.52, 4535.48) * mm});
            skLineSegment(sketch, "E648", {"start": v(-432.52, 4535.48) * mm, "end": v(-437.64, 4524.9) * mm});
            skLineSegment(sketch, "E649", {"start": v(-437.64, 4524.9) * mm, "end": v(-441.55, 4513.49) * mm});
            skLineSegment(sketch, "E650", {"start": v(-441.55, 4513.49) * mm, "end": v(-444.17, 4501.26) * mm});
            skLineSegment(sketch, "E651", {"start": v(-444.17, 4501.26) * mm, "end": v(-445.38, 4488.23) * mm});
            skLineSegment(sketch, "E652", {"start": v(-445.38, 4488.23) * mm, "end": v(-444.73, 4465.31) * mm});
            skLineSegment(sketch, "E653", {"start": v(-444.73, 4465.31) * mm, "end": v(-445.12, 4456.68) * mm});
            skLineSegment(sketch, "E654", {"start": v(-445.12, 4456.68) * mm, "end": v(-446.19, 4448.48) * mm});
            skLineSegment(sketch, "E655", {"start": v(-446.19, 4448.48) * mm, "end": v(-447.92, 4440.7) * mm});
            skLineSegment(sketch, "E656", {"start": v(-447.92, 4440.7) * mm, "end": v(-450.28, 4433.28) * mm});
            skLineSegment(sketch, "E657", {"start": v(-450.28, 4433.28) * mm, "end": v(-453.23, 4426.21) * mm});
            skLineSegment(sketch, "E658", {"start": v(-453.23, 4426.21) * mm, "end": v(-456.74, 4419.41) * mm});
            skLineSegment(sketch, "E659", {"start": v(-456.74, 4419.41) * mm, "end": v(-460.77, 4412.9) * mm});
            skLineSegment(sketch, "E660", {"start": v(-460.77, 4412.9) * mm, "end": v(-465.3, 4406.6) * mm});
            skLineSegment(sketch, "E661", {"start": v(-465.3, 4406.6) * mm, "end": v(-470.29, 4400.49) * mm});
            skLineSegment(sketch, "E662", {"start": v(-470.29, 4400.49) * mm, "end": v(-475.7, 4394.52) * mm});
            skLineSegment(sketch, "E663", {"start": v(-475.7, 4394.52) * mm, "end": v(-481.5, 4388.67) * mm});
            skLineSegment(sketch, "E664", {"start": v(-481.5, 4388.67) * mm, "end": v(-494.43, 4376.33) * mm});
            skLineSegment(sketch, "E665", {"start": v(-494.43, 4376.33) * mm, "end": v(-500.57, 4369.57) * mm});
            skLineSegment(sketch, "E666", {"start": v(-500.57, 4369.57) * mm, "end": v(-506.05, 4362.6) * mm});
            skLineSegment(sketch, "E667", {"start": v(-506.05, 4362.6) * mm, "end": v(-510.88, 4355.42) * mm});
            skLineSegment(sketch, "E668", {"start": v(-510.88, 4355.42) * mm, "end": v(-515.05, 4348.02) * mm});
            skLineSegment(sketch, "E669", {"start": v(-515.05, 4348.02) * mm, "end": v(-518.54, 4340.4) * mm});
            skLineSegment(sketch, "E670", {"start": v(-518.54, 4340.4) * mm, "end": v(-521.35, 4332.55) * mm});
            skLineSegment(sketch, "E671", {"start": v(-521.35, 4332.55) * mm, "end": v(-523.47, 4324.47) * mm});
            skLineSegment(sketch, "E672", {"start": v(-523.47, 4324.47) * mm, "end": v(-524.9, 4316.15) * mm});
            skLineSegment(sketch, "E673", {"start": v(-524.9, 4316.15) * mm, "end": v(-525.61, 4307.59) * mm});
            skLineSegment(sketch, "E674", {"start": v(-525.61, 4307.59) * mm, "end": v(-525.62, 4298.79) * mm});
            skLineSegment(sketch, "E675", {"start": v(-525.62, 4298.79) * mm, "end": v(-524.9, 4289.73) * mm});
            skLineSegment(sketch, "E676", {"start": v(-524.9, 4289.73) * mm, "end": v(-523.45, 4280.43) * mm});
            skLineSegment(sketch, "E677", {"start": v(-523.45, 4280.43) * mm, "end": v(-519.99, 4265.65) * mm});
            skLineSegment(sketch, "E678", {"start": v(-519.99, 4265.65) * mm, "end": v(-518.93, 4260.33) * mm});
            skLineSegment(sketch, "E679", {"start": v(-518.93, 4260.33) * mm, "end": v(-518.06, 4254.89) * mm});
            skLineSegment(sketch, "E680", {"start": v(-518.06, 4254.89) * mm, "end": v(-517.41, 4249.4) * mm});
            skLineSegment(sketch, "E681", {"start": v(-517.41, 4249.4) * mm, "end": v(-516.98, 4243.86) * mm});
            skLineSegment(sketch, "E682", {"start": v(-516.98, 4243.86) * mm, "end": v(-516.76, 4238.3) * mm});
            skLineSegment(sketch, "E683", {"start": v(-516.76, 4238.3) * mm, "end": v(-516.77, 4232.76) * mm});
            skLineSegment(sketch, "E684", {"start": v(-516.77, 4232.76) * mm, "end": v(-517, 4227.25) * mm});
            skLineSegment(sketch, "E685", {"start": v(-517, 4227.25) * mm, "end": v(-517.48, 4221.8) * mm});
            skLineSegment(sketch, "E686", {"start": v(-517.48, 4221.8) * mm, "end": v(-518.2, 4216.43) * mm});
            skLineSegment(sketch, "E687", {"start": v(-518.2, 4216.43) * mm, "end": v(-519.17, 4211.18) * mm});
            skLineSegment(sketch, "E688", {"start": v(-519.17, 4211.18) * mm, "end": v(-548.04, 4074.2) * mm});
            skLineSegment(sketch, "E689", {"start": v(-548.04, 4074.2) * mm, "end": v(-565.02, 3999.74) * mm});
            skLineSegment(sketch, "E690", {"start": v(-565.02, 3999.74) * mm, "end": v(-586.92, 3913.99) * mm});
            skLineSegment(sketch, "E691", {"start": v(-586.92, 3913.99) * mm, "end": v(-589.56, 3902.16) * mm});
            skLineSegment(sketch, "E692", {"start": v(-589.56, 3902.16) * mm, "end": v(-591.82, 3890.36) * mm});
            skLineSegment(sketch, "E693", {"start": v(-591.82, 3890.36) * mm, "end": v(-593.72, 3878.56) * mm});
            skLineSegment(sketch, "E694", {"start": v(-593.72, 3878.56) * mm, "end": v(-595.25, 3866.79) * mm});
            skLineSegment(sketch, "E695", {"start": v(-595.25, 3866.79) * mm, "end": v(-596.44, 3855.04) * mm});
            skLineSegment(sketch, "E696", {"start": v(-596.44, 3855.04) * mm, "end": v(-597.29, 3843.32) * mm});
            skLineSegment(sketch, "E697", {"start": v(-597.29, 3843.32) * mm, "end": v(-597.83, 3831.6) * mm});
            skLineSegment(sketch, "E698", {"start": v(-597.83, 3831.6) * mm, "end": v(-598.03, 3819.9) * mm});
            skLineSegment(sketch, "E699", {"start": v(-598.03, 3819.9) * mm, "end": v(-597.94, 3808.22) * mm});
            skLineSegment(sketch, "E700", {"start": v(-597.94, 3808.22) * mm, "end": v(-597.55, 3796.58) * mm});
            skLineSegment(sketch, "E701", {"start": v(-597.55, 3796.58) * mm, "end": v(-596.88, 3784.99) * mm});
            skLineSegment(sketch, "E702", {"start": v(-596.88, 3784.99) * mm, "end": v(-595.93, 3773.39) * mm});
            skLineSegment(sketch, "E703", {"start": v(-595.93, 3773.39) * mm, "end": v(-594.73, 3761.83) * mm});
            skLineSegment(sketch, "E704", {"start": v(-594.73, 3761.83) * mm, "end": v(-593.27, 3750.31) * mm});
            skLineSegment(sketch, "E705", {"start": v(-593.27, 3750.31) * mm, "end": v(-591.57, 3738.82) * mm});
            skLineSegment(sketch, "E706", {"start": v(-591.57, 3738.82) * mm, "end": v(-589.64, 3727.37) * mm});
            skLineSegment(sketch, "E707", {"start": v(-589.64, 3727.37) * mm, "end": v(-587.49, 3715.95) * mm});
            skLineSegment(sketch, "E708", {"start": v(-587.49, 3715.95) * mm, "end": v(-585.13, 3704.56) * mm});
            skLineSegment(sketch, "E709", {"start": v(-585.13, 3704.56) * mm, "end": v(-579.83, 3681.91) * mm});
            skLineSegment(sketch, "E710", {"start": v(-579.83, 3681.91) * mm, "end": v(-572.87, 3655.76) * mm});
            skLineSegment(sketch, "E711", {"start": v(-572.87, 3655.76) * mm, "end": v(-560.24, 3611.25) * mm});
            skLineSegment(sketch, "E712", {"start": v(-560.24, 3611.25) * mm, "end": v(-452.25, 3272.9) * mm});
            skLineSegment(sketch, "E713", {"start": v(-452.25, 3272.9) * mm, "end": v(-436.73, 3220.8) * mm});
            skLineSegment(sketch, "E714", {"start": v(-436.73, 3220.8) * mm, "end": v(-419.3, 3157.83) * mm});
            skLineSegment(sketch, "E715", {"start": v(-419.3, 3157.83) * mm, "end": v(-394.9, 3062.95) * mm});
            skLineSegment(sketch, "E716", {"start": v(-394.9, 3062.95) * mm, "end": v(-393.59, 3057.1) * mm});
            skLineSegment(sketch, "E717", {"start": v(-393.59, 3057.1) * mm, "end": v(-392.54, 3051.2) * mm});
            skLineSegment(sketch, "E718", {"start": v(-392.54, 3051.2) * mm, "end": v(-391.7, 3045.25) * mm});
            skLineSegment(sketch, "E719", {"start": v(-391.7, 3045.25) * mm, "end": v(-391.06, 3039.26) * mm});
            skLineSegment(sketch, "E720", {"start": v(-391.06, 3039.26) * mm, "end": v(-390.56, 3033.22) * mm});
            skLineSegment(sketch, "E721", {"start": v(-390.56, 3033.22) * mm, "end": v(-390.18, 3027.2) * mm});
            skLineSegment(sketch, "E722", {"start": v(-390.18, 3027.2) * mm, "end": v(-389.08, 3003.12) * mm});
            skLineSegment(sketch, "E723", {"start": v(-389.08, 3003.12) * mm, "end": v(-388.35, 2991.2) * mm});
            skLineSegment(sketch, "E724", {"start": v(-388.35, 2991.2) * mm, "end": v(-390.7, 2987.32) * mm});
            skLineSegment(sketch, "E725", {"start": v(-390.7, 2987.32) * mm, "end": v(-395.91, 2979.15) * mm});
            skLineSegment(sketch, "E726", {"start": v(-395.91, 2979.15) * mm, "end": v(-401.37, 2970.45) * mm});
            skLineSegment(sketch, "E727", {"start": v(-401.37, 2970.45) * mm, "end": v(-404, 2965.9) * mm});
            skLineSegment(sketch, "E728", {"start": v(-404, 2965.9) * mm, "end": v(-406.46, 2961.2) * mm});
            skLineSegment(sketch, "E729", {"start": v(-406.46, 2961.2) * mm, "end": v(-408.69, 2956.4) * mm});
            skLineSegment(sketch, "E730", {"start": v(-408.69, 2956.4) * mm, "end": v(-410.61, 2951.43) * mm});
            skLineSegment(sketch, "E731", {"start": v(-410.61, 2951.43) * mm, "end": v(-411.92, 2946.81) * mm});
            skLineSegment(sketch, "E732", {"start": v(-411.92, 2946.81) * mm, "end": v(-412.78, 2942.06) * mm});
            skLineSegment(sketch, "E733", {"start": v(-412.78, 2942.06) * mm, "end": v(-413.32, 2937.17) * mm});
            skLineSegment(sketch, "E734", {"start": v(-413.32, 2937.17) * mm, "end": v(-414.14, 2922.26) * mm});
            skLineSegment(sketch, "E735", {"start": v(-414.14, 2922.26) * mm, "end": v(-414.53, 2917.3) * mm});
            skLineSegment(sketch, "E736", {"start": v(-414.53, 2917.3) * mm, "end": v(-415.2, 2912.42) * mm});
            skLineSegment(sketch, "E737", {"start": v(-415.2, 2912.42) * mm, "end": v(-416.24, 2907.66) * mm});
            skLineSegment(sketch, "E738", {"start": v(-416.24, 2907.66) * mm, "end": v(-451.7, 2782.54) * mm});
            skLineSegment(sketch, "E739", {"start": v(-451.7, 2782.54) * mm, "end": v(-465.84, 2730.26) * mm});
            skLineSegment(sketch, "E740", {"start": v(-465.84, 2730.26) * mm, "end": v(-473.62, 2698.73) * mm});
            skLineSegment(sketch, "E741", {"start": v(-473.62, 2698.73) * mm, "end": v(-474.85, 2692.56) * mm});
            skLineSegment(sketch, "E742", {"start": v(-474.85, 2692.56) * mm, "end": v(-475.69, 2686.2) * mm});
            skLineSegment(sketch, "E743", {"start": v(-475.69, 2686.2) * mm, "end": v(-476.15, 2679.67) * mm});
            skLineSegment(sketch, "E744", {"start": v(-476.15, 2679.67) * mm, "end": v(-476.24, 2673.04) * mm});
            skLineSegment(sketch, "E745", {"start": v(-476.24, 2673.04) * mm, "end": v(-475.99, 2666.35) * mm});
            skLineSegment(sketch, "E746", {"start": v(-475.99, 2666.35) * mm, "end": v(-475.39, 2659.66) * mm});
            skLineSegment(sketch, "E747", {"start": v(-475.39, 2659.66) * mm, "end": v(-474.47, 2653) * mm});
            skLineSegment(sketch, "E748", {"start": v(-474.47, 2653) * mm, "end": v(-473.23, 2646.45) * mm});
            skLineSegment(sketch, "E749", {"start": v(-473.23, 2646.45) * mm, "end": v(-471.68, 2640.03) * mm});
            skLineSegment(sketch, "E750", {"start": v(-471.68, 2640.03) * mm, "end": v(-469.85, 2633.8) * mm});
            skLineSegment(sketch, "E751", {"start": v(-469.85, 2633.8) * mm, "end": v(-464.35, 2618.4) * mm});
            skLineSegment(sketch, "E752", {"start": v(-464.35, 2618.4) * mm, "end": v(-461.37, 2609) * mm});
            skLineSegment(sketch, "E753", {"start": v(-461.37, 2609) * mm, "end": v(-458.81, 2599.58) * mm});
            skLineSegment(sketch, "E754", {"start": v(-458.81, 2599.58) * mm, "end": v(-456.68, 2590.17) * mm});
            skLineSegment(sketch, "E755", {"start": v(-456.68, 2590.17) * mm, "end": v(-454.96, 2580.77) * mm});
            skLineSegment(sketch, "E756", {"start": v(-454.96, 2580.77) * mm, "end": v(-453.66, 2571.37) * mm});
            skLineSegment(sketch, "E757", {"start": v(-453.66, 2571.37) * mm, "end": v(-452.78, 2562) * mm});
            skLineSegment(sketch, "E758", {"start": v(-452.78, 2562) * mm, "end": v(-452.33, 2552.66) * mm});
            skLineSegment(sketch, "E759", {"start": v(-452.33, 2552.66) * mm, "end": v(-452.3, 2543.35) * mm});
            skLineSegment(sketch, "E760", {"start": v(-452.3, 2543.35) * mm, "end": v(-452.68, 2534.07) * mm});
            skLineSegment(sketch, "E761", {"start": v(-452.68, 2534.07) * mm, "end": v(-453.5, 2524.84) * mm});
            skLineSegment(sketch, "E762", {"start": v(-453.5, 2524.84) * mm, "end": v(-454.74, 2515.67) * mm});
            skLineSegment(sketch, "E763", {"start": v(-454.74, 2515.67) * mm, "end": v(-456.4, 2506.55) * mm});
            skLineSegment(sketch, "E764", {"start": v(-456.4, 2506.55) * mm, "end": v(-458.49, 2497.49) * mm});
            skLineSegment(sketch, "E765", {"start": v(-458.49, 2497.49) * mm, "end": v(-461, 2488.51) * mm});
            skLineSegment(sketch, "E766", {"start": v(-461, 2488.51) * mm, "end": v(-463.94, 2479.6) * mm});
            skLineSegment(sketch, "E767", {"start": v(-463.94, 2479.6) * mm, "end": v(-488.63, 2417.64) * mm});
            skLineSegment(sketch, "E768", {"start": v(-488.63, 2417.64) * mm, "end": v(-509.05, 2364.22) * mm});
            skLineSegment(sketch, "E769", {"start": v(-509.05, 2364.22) * mm, "end": v(-523.52, 2323.91) * mm});
            skLineSegment(sketch, "E770", {"start": v(-523.52, 2323.91) * mm, "end": v(-537.08, 2283.35) * mm});
            skLineSegment(sketch, "E771", {"start": v(-537.08, 2283.35) * mm, "end": v(-545.54, 2256.14) * mm});
            skLineSegment(sketch, "E772", {"start": v(-545.54, 2256.14) * mm, "end": v(-553.46, 2228.78) * mm});
            skLineSegment(sketch, "E773", {"start": v(-553.46, 2228.78) * mm, "end": v(-560.81, 2201.25) * mm});
            skLineSegment(sketch, "E774", {"start": v(-560.81, 2201.25) * mm, "end": v(-567.52, 2173.6) * mm});
            skLineSegment(sketch, "E775", {"start": v(-567.52, 2173.6) * mm, "end": v(-573.56, 2145.64) * mm});
            skLineSegment(sketch, "E776", {"start": v(-573.56, 2145.64) * mm, "end": v(-578.87, 2117.54) * mm});
            skLineSegment(sketch, "E777", {"start": v(-578.87, 2117.54) * mm, "end": v(-580.62, 2106.8) * mm});
            skLineSegment(sketch, "E778", {"start": v(-580.62, 2106.8) * mm, "end": v(-582.15, 2096.03) * mm});
            skLineSegment(sketch, "E779", {"start": v(-582.15, 2096.03) * mm, "end": v(-583.48, 2085.22) * mm});
            skLineSegment(sketch, "E780", {"start": v(-583.48, 2085.22) * mm, "end": v(-585.65, 2063.5) * mm});
            skLineSegment(sketch, "E781", {"start": v(-585.65, 2063.5) * mm, "end": v(-592.2, 1965.22) * mm});
            skLineSegment(sketch, "E782", {"start": v(-592.2, 1965.22) * mm, "end": v(-594.13, 1943.48) * mm});
            skLineSegment(sketch, "E783", {"start": v(-594.13, 1943.48) * mm, "end": v(-596.67, 1921.87) * mm});
            skLineSegment(sketch, "E784", {"start": v(-596.67, 1921.87) * mm, "end": v(-598.23, 1911.12) * mm});
            skLineSegment(sketch, "E785", {"start": v(-598.23, 1911.12) * mm, "end": v(-604.2, 1877.82) * mm});
            skLineSegment(sketch, "E786", {"start": v(-604.2, 1877.82) * mm, "end": v(-605.83, 1865.77) * mm});
            skLineSegment(sketch, "E787", {"start": v(-605.83, 1865.77) * mm, "end": v(-607.03, 1853.63) * mm});
            skLineSegment(sketch, "E788", {"start": v(-607.03, 1853.63) * mm, "end": v(-607.88, 1841.43) * mm});
            skLineSegment(sketch, "E789", {"start": v(-607.88, 1841.43) * mm, "end": v(-608.43, 1829.18) * mm});
            skLineSegment(sketch, "E790", {"start": v(-608.43, 1829.18) * mm, "end": v(-609.26, 1779.9) * mm});
            skLineSegment(sketch, "E791", {"start": v(-609.26, 1779.9) * mm, "end": v(-609.87, 1755.26) * mm});
            skLineSegment(sketch, "E792", {"start": v(-609.87, 1755.26) * mm, "end": v(-610.48, 1743.02) * mm});
            skLineSegment(sketch, "E793", {"start": v(-610.48, 1743.02) * mm, "end": v(-611.4, 1730.83) * mm});
            skLineSegment(sketch, "E794", {"start": v(-611.4, 1730.83) * mm, "end": v(-612.71, 1718.72) * mm});
            skLineSegment(sketch, "E795", {"start": v(-612.71, 1718.72) * mm, "end": v(-614.47, 1706.7) * mm});
            skLineSegment(sketch, "E796", {"start": v(-614.47, 1706.7) * mm, "end": v(-616.75, 1694.77) * mm});
            skLineSegment(sketch, "E797", {"start": v(-616.75, 1694.77) * mm, "end": v(-619.64, 1682.96) * mm});
            skLineSegment(sketch, "E798", {"start": v(-619.64, 1682.96) * mm, "end": v(-623.2, 1671.3) * mm});
            skLineSegment(sketch, "E799", {"start": v(-623.2, 1671.3) * mm, "end": v(-627.53, 1659.78) * mm});
            skLineSegment(sketch, "E800", {"start": v(-627.53, 1659.78) * mm, "end": v(-632.66, 1648.4) * mm});
            skLineSegment(sketch, "E801", {"start": v(-632.66, 1648.4) * mm, "end": v(-638.7, 1637.2) * mm});
            skLineSegment(sketch, "E802", {"start": v(-638.7, 1637.2) * mm, "end": v(-645.72, 1626.19) * mm});
            skLineSegment(sketch, "E803", {"start": v(-645.72, 1626.19) * mm, "end": v(-653.78, 1615.39) * mm});
            skLineSegment(sketch, "E804", {"start": v(-653.78, 1615.39) * mm, "end": v(-654.9, 1613.3) * mm});
            skLineSegment(sketch, "E805", {"start": v(-654.9, 1613.3) * mm, "end": v(-655.5, 1610.75) * mm});
            skLineSegment(sketch, "E806", {"start": v(-655.5, 1610.75) * mm, "end": v(-655.74, 1607.93) * mm});
            skLineSegment(sketch, "E807", {"start": v(-655.74, 1607.93) * mm, "end": v(-655.77, 1602.25) * mm});
            skLineSegment(sketch, "E808", {"start": v(-655.77, 1602.25) * mm, "end": v(-655.98, 1593.5) * mm});
            skLineSegment(sketch, "E809", {"start": v(-655.98, 1593.5) * mm, "end": v(-656.4, 1584.82) * mm});
            skLineSegment(sketch, "E810", {"start": v(-656.4, 1584.82) * mm, "end": v(-657, 1576.2) * mm});
            skLineSegment(sketch, "E811", {"start": v(-657, 1576.2) * mm, "end": v(-657.8, 1567.62) * mm});
            skLineSegment(sketch, "E812", {"start": v(-657.8, 1567.62) * mm, "end": v(-658.77, 1559.08) * mm});
            skLineSegment(sketch, "E813", {"start": v(-658.77, 1559.08) * mm, "end": v(-659.92, 1550.57) * mm});
            skLineSegment(sketch, "E814", {"start": v(-659.92, 1550.57) * mm, "end": v(-661.24, 1542.1) * mm});
            skLineSegment(sketch, "E815", {"start": v(-661.24, 1542.1) * mm, "end": v(-662.71, 1533.64) * mm});
            skLineSegment(sketch, "E816", {"start": v(-662.71, 1533.64) * mm, "end": v(-664.34, 1525.2) * mm});
            skLineSegment(sketch, "E817", {"start": v(-664.34, 1525.2) * mm, "end": v(-668.02, 1508.3) * mm});
            skLineSegment(sketch, "E818", {"start": v(-668.02, 1508.3) * mm, "end": v(-672.24, 1491.39) * mm});
            skLineSegment(sketch, "E819", {"start": v(-672.24, 1491.39) * mm, "end": v(-682.26, 1455.7) * mm});
            skLineSegment(sketch, "E820", {"start": v(-682.26, 1455.7) * mm, "end": v(-684.75, 1445.54) * mm});
            skLineSegment(sketch, "E821", {"start": v(-684.75, 1445.54) * mm, "end": v(-686.95, 1435.28) * mm});
            skLineSegment(sketch, "E822", {"start": v(-686.95, 1435.28) * mm, "end": v(-688.87, 1424.92) * mm});
            skLineSegment(sketch, "E823", {"start": v(-688.87, 1424.92) * mm, "end": v(-690.56, 1414.47) * mm});
            skLineSegment(sketch, "E824", {"start": v(-690.56, 1414.47) * mm, "end": v(-692.02, 1403.95) * mm});
            skLineSegment(sketch, "E825", {"start": v(-692.02, 1403.95) * mm, "end": v(-694.4, 1382.67) * mm});
            skLineSegment(sketch, "E826", {"start": v(-694.4, 1382.67) * mm, "end": v(-701.44, 1284.06) * mm});
            skLineSegment(sketch, "E827", {"start": v(-701.44, 1284.06) * mm, "end": v(-703.46, 1261.72) * mm});
            skLineSegment(sketch, "E828", {"start": v(-703.46, 1261.72) * mm, "end": v(-710.88, 1261.28) * mm});
            skLineSegment(sketch, "E829", {"start": v(-710.88, 1261.28) * mm, "end": v(-716.97, 1259.36) * mm});
            skLineSegment(sketch, "E830", {"start": v(-716.97, 1259.36) * mm, "end": v(-721.89, 1256.1) * mm});
            skLineSegment(sketch, "E831", {"start": v(-721.89, 1256.1) * mm, "end": v(-725.76, 1251.67) * mm});
            skLineSegment(sketch, "E832", {"start": v(-725.76, 1251.67) * mm, "end": v(-728.73, 1246.22) * mm});
            skLineSegment(sketch, "E833", {"start": v(-728.73, 1246.22) * mm, "end": v(-730.93, 1239.92) * mm});
            skLineSegment(sketch, "E834", {"start": v(-730.93, 1239.92) * mm, "end": v(-732.5, 1232.92) * mm});
            skLineSegment(sketch, "E835", {"start": v(-732.5, 1232.92) * mm, "end": v(-733.58, 1225.38) * mm});
            skLineSegment(sketch, "E836", {"start": v(-733.58, 1225.38) * mm, "end": v(-734.29, 1217.45) * mm});
            skLineSegment(sketch, "E837", {"start": v(-734.29, 1217.45) * mm, "end": v(-735.42, 1195.92) * mm});
            skLineSegment(sketch, "E838", {"start": v(-735.42, 1195.92) * mm, "end": v(-735.96, 1187) * mm});
            skLineSegment(sketch, "E839", {"start": v(-735.96, 1187) * mm, "end": v(-736.34, 1182.57) * mm});
            skLineSegment(sketch, "E840", {"start": v(-736.34, 1182.57) * mm, "end": v(-736.83, 1178.15) * mm});
            skLineSegment(sketch, "E841", {"start": v(-736.83, 1178.15) * mm, "end": v(-737.45, 1173.74) * mm});
            skLineSegment(sketch, "E842", {"start": v(-737.45, 1173.74) * mm, "end": v(-858.21, 421.6) * mm});
            skLineSegment(sketch, "E843", {"start": v(-858.21, 421.6) * mm, "end": v(-885.44, 276.1) * mm});
            skLineSegment(sketch, "E844", {"start": v(-885.44, 276.1) * mm, "end": v(-902.32, 183.45) * mm});
            skLineSegment(sketch, "E845", {"start": v(-902.32, 183.45) * mm, "end": v(-910.78, 130.33) * mm});
            skLineSegment(sketch, "E846", {"start": v(-910.78, 130.33) * mm, "end": v(-913.38, 116.28) * mm});
            skLineSegment(sketch, "E847", {"start": v(-913.38, 116.28) * mm, "end": v(-917.08, 101.94) * mm});
            skLineSegment(sketch, "E848", {"start": v(-917.08, 101.94) * mm, "end": v(-921.82, 87.37) * mm});
            skLineSegment(sketch, "E849", {"start": v(-921.82, 87.37) * mm, "end": v(-927.55, 72.68) * mm});
            skLineSegment(sketch, "E850", {"start": v(-927.55, 72.68) * mm, "end": v(-934.22, 57.96) * mm});
            skLineSegment(sketch, "E851", {"start": v(-934.22, 57.96) * mm, "end": v(-941.77, 43.29) * mm});
            skLineSegment(sketch, "E852", {"start": v(-941.77, 43.29) * mm, "end": v(-950.15, 28.77) * mm});
            skLineSegment(sketch, "E853", {"start": v(-950.15, 28.77) * mm, "end": v(-959.3, 14.48) * mm});
            skLineSegment(sketch, "E854", {"start": v(-959.3, 14.48) * mm, "end": v(-969.19, 0.5) * mm});
            skLineSegment(sketch, "E855", {"start": v(-969.19, 0.5) * mm, "end": v(-979.76, -13.04) * mm});
            skLineSegment(sketch, "E856", {"start": v(-979.76, -13.04) * mm, "end": v(-990.95, -26.08) * mm});
            skLineSegment(sketch, "E857", {"start": v(-990.95, -26.08) * mm, "end": v(-1002.7, -38.53) * mm});
            skLineSegment(sketch, "E858", {"start": v(-1002.7, -38.53) * mm, "end": v(-1014.99, -50.3) * mm});
            skLineSegment(sketch, "E859", {"start": v(-1014.99, -50.3) * mm, "end": v(-1027.75, -61.3) * mm});
            skLineSegment(sketch, "E860", {"start": v(-1027.75, -61.3) * mm, "end": v(-1040.9, -71.4) * mm});
            skLineSegment(sketch, "E861", {"start": v(-1040.9, -71.4) * mm, "end": v(-1054.45, -80.57) * mm});
            skLineSegment(sketch, "E862", {"start": v(-1054.45, -80.57) * mm, "end": v(-1068.27, -88.66) * mm});
            skLineSegment(sketch, "E863", {"start": v(-1068.27, -88.66) * mm, "end": v(-1082.37, -95.66) * mm});
            skLineSegment(sketch, "E864", {"start": v(-1082.37, -95.66) * mm, "end": v(-1096.68, -101.41) * mm});
            skLineSegment(sketch, "E865", {"start": v(-1096.68, -101.41) * mm, "end": v(-1111.14, -105.84) * mm});
            skLineSegment(sketch, "E866", {"start": v(-1111.14, -105.84) * mm, "end": v(-1125.7, -108.86) * mm});
            skLineSegment(sketch, "E867", {"start": v(-1125.7, -108.86) * mm, "end": v(-1152.66, -112.99) * mm});
            skLineSegment(sketch, "E868", {"start": v(-2213.01, -2754.08) * mm, "end": v(-5633.3, -233.14) * mm});
            skLineSegment(sketch, "E869", {"start": v(-5633.3, -233.14) * mm, "end": v(-1269.94, -233.14) * mm});
            skLineSegment(sketch, "E870", {"start": v(-1269.94, -233.14) * mm, "end": v(-1266.33, -220) * mm});
            skLineSegment(sketch, "E871", {"start": v(-1266.33, -220) * mm, "end": v(-1261.4, -201.14) * mm});
            skLineSegment(sketch, "E872", {"start": v(-1261.4, -201.14) * mm, "end": v(-1259.71, -195.12) * mm});
            skLineSegment(sketch, "E873", {"start": v(-1259.71, -195.12) * mm, "end": v(-1257.91, -189.23) * mm});
            skLineSegment(sketch, "E874", {"start": v(-1257.91, -189.23) * mm, "end": v(-1255.97, -183.5) * mm});
            skLineSegment(sketch, "E875", {"start": v(-1255.97, -183.5) * mm, "end": v(-1253.83, -177.93) * mm});
            skLineSegment(sketch, "E876", {"start": v(-1253.83, -177.93) * mm, "end": v(-1251.44, -172.53) * mm});
            skLineSegment(sketch, "E877", {"start": v(-1251.44, -172.53) * mm, "end": v(-1248.78, -167.3) * mm});
            skLineSegment(sketch, "E878", {"start": v(-1248.78, -167.3) * mm, "end": v(-1243.19, -158.36) * mm});
            skLineSegment(sketch, "E879", {"start": v(-1243.19, -158.36) * mm, "end": v(-1236.94, -150.49) * mm});
            skLineSegment(sketch, "E880", {"start": v(-1236.94, -150.49) * mm, "end": v(-1230.08, -143.6) * mm});
            skLineSegment(sketch, "E881", {"start": v(-1230.08, -143.6) * mm, "end": v(-1222.71, -137.65) * mm});
            skLineSegment(sketch, "E882", {"start": v(-1222.71, -137.65) * mm, "end": v(-1214.89, -132.53) * mm});
            skLineSegment(sketch, "E883", {"start": v(-1214.89, -132.53) * mm, "end": v(-1206.65, -128.15) * mm});
            skLineSegment(sketch, "E884", {"start": v(-1206.65, -128.15) * mm, "end": v(-1198.1, -124.44) * mm});
            skLineSegment(sketch, "E885", {"start": v(-1198.1, -124.44) * mm, "end": v(-1189.27, -121.31) * mm});
            skLineSegment(sketch, "E886", {"start": v(-1189.27, -121.31) * mm, "end": v(-1180.25, -118.69) * mm});
            skLineSegment(sketch, "E887", {"start": v(-1180.25, -118.69) * mm, "end": v(-1171.1, -116.48) * mm});
            skLineSegment(sketch, "E888", {"start": v(-1171.1, -116.48) * mm, "end": v(-1161.88, -114.6) * mm});
            skLineSegment(sketch, "E889", {"start": v(-1161.88, -114.6) * mm, "end": v(-1152.66, -112.99) * mm});
            skLineSegment(sketch, "E890", {"start": v(-503.47, -232.52) * mm, "end": v(549.38, -233.12) * mm});
            skLineSegment(sketch, "E891", {"start": v(549.38, -233.12) * mm, "end": v(552.25, -225.12) * mm});
            skLineSegment(sketch, "E892", {"start": v(552.25, -225.12) * mm, "end": v(557.18, -209.89) * mm});
            skLineSegment(sketch, "E893", {"start": v(557.18, -209.89) * mm, "end": v(561.5, -195.82) * mm});
            skLineSegment(sketch, "E894", {"start": v(561.5, -195.82) * mm, "end": v(563.66, -189.26) * mm});
            skLineSegment(sketch, "E895", {"start": v(563.66, -189.26) * mm, "end": v(565.91, -183.06) * mm});
            skLineSegment(sketch, "E896", {"start": v(565.91, -183.06) * mm, "end": v(568.36, -177.22) * mm});
            skLineSegment(sketch, "E897", {"start": v(568.36, -177.22) * mm, "end": v(571.07, -171.76) * mm});
            skLineSegment(sketch, "E898", {"start": v(571.07, -171.76) * mm, "end": v(574.13, -166.7) * mm});
            skLineSegment(sketch, "E899", {"start": v(574.13, -166.7) * mm, "end": v(577.63, -162.08) * mm});
            skLineSegment(sketch, "E900", {"start": v(577.63, -162.08) * mm, "end": v(583.75, -155.18) * mm});
            skLineSegment(sketch, "E901", {"start": v(583.75, -155.18) * mm, "end": v(590.13, -148.5) * mm});
            skLineSegment(sketch, "E902", {"start": v(590.13, -148.5) * mm, "end": v(596.74, -142.03) * mm});
            skLineSegment(sketch, "E903", {"start": v(596.74, -142.03) * mm, "end": v(603.38, -135.8) * mm});
            skLineSegment(sketch, "E904", {"start": v(603.38, -135.8) * mm, "end": v(617.4, -123.42) * mm});
            skLineSegment(sketch, "E905", {"start": v(617.4, -123.42) * mm, "end": v(645.93, -99.1) * mm});
            skLineSegment(sketch, "E906", {"start": v(645.93, -99.1) * mm, "end": v(652.63, -92.79) * mm});
            skLineSegment(sketch, "E907", {"start": v(652.63, -92.79) * mm, "end": v(659.71, -85.9) * mm});
            skLineSegment(sketch, "E908", {"start": v(659.71, -85.9) * mm, "end": v(677.35, -68.42) * mm});
            skLineSegment(sketch, "E909", {"start": v(677.35, -68.42) * mm, "end": v(686.02, -59.36) * mm});
            skLineSegment(sketch, "E910", {"start": v(686.02, -59.36) * mm, "end": v(694.45, -50.23) * mm});
            skLineSegment(sketch, "E911", {"start": v(694.45, -50.23) * mm, "end": v(702.54, -40.96) * mm});
            skLineSegment(sketch, "E912", {"start": v(702.54, -40.96) * mm, "end": v(710.32, -31.54) * mm});
            skLineSegment(sketch, "E913", {"start": v(710.32, -31.54) * mm, "end": v(717.62, -22) * mm});
            skLineSegment(sketch, "E914", {"start": v(717.62, -22) * mm, "end": v(724.45, -12.21) * mm});
            skLineSegment(sketch, "E915", {"start": v(724.45, -12.21) * mm, "end": v(730.77, -2.24) * mm});
            skLineSegment(sketch, "E916", {"start": v(730.77, -2.24) * mm, "end": v(736.49, 7.94) * mm});
            skLineSegment(sketch, "E917", {"start": v(736.49, 7.94) * mm, "end": v(741.6, 18.35) * mm});
            skLineSegment(sketch, "E918", {"start": v(741.6, 18.35) * mm, "end": v(746.02, 29.13) * mm});
            skLineSegment(sketch, "E919", {"start": v(746.02, 29.13) * mm, "end": v(749.68, 40.11) * mm});
            skLineSegment(sketch, "E920", {"start": v(749.68, 40.11) * mm, "end": v(752.57, 51.44) * mm});
            skLineSegment(sketch, "E921", {"start": v(752.57, 51.44) * mm, "end": v(754.6, 63.08) * mm});
            skLineSegment(sketch, "E922", {"start": v(754.6, 63.08) * mm, "end": v(755.78, 75.11) * mm});
            skLineSegment(sketch, "E923", {"start": v(755.78, 75.11) * mm, "end": v(755.93, 87.52) * mm});
            skLineSegment(sketch, "E924", {"start": v(755.93, 87.52) * mm, "end": v(755.12, 100.31) * mm});
            skLineSegment(sketch, "E925", {"start": v(755.12, 100.31) * mm, "end": v(753.28, 113.53) * mm});
            skLineSegment(sketch, "E926", {"start": v(753.28, 113.53) * mm, "end": v(750.29, 127.17) * mm});
            skLineSegment(sketch, "E927", {"start": v(750.29, 127.17) * mm, "end": v(746.14, 141.32) * mm});
            skLineSegment(sketch, "E928", {"start": v(746.14, 141.32) * mm, "end": v(745.34, 145.48) * mm});
            skLineSegment(sketch, "E929", {"start": v(745.34, 145.48) * mm, "end": v(745.43, 150) * mm});
            skLineSegment(sketch, "E930", {"start": v(745.43, 150) * mm, "end": v(746.3, 154.71) * mm});
            skLineSegment(sketch, "E931", {"start": v(746.3, 154.71) * mm, "end": v(747.76, 159.63) * mm});
            skLineSegment(sketch, "E932", {"start": v(747.76, 159.63) * mm, "end": v(749.63, 164.7) * mm});
            skLineSegment(sketch, "E933", {"start": v(749.63, 164.7) * mm, "end": v(756, 180.27) * mm});
            skLineSegment(sketch, "E934", {"start": v(756, 180.27) * mm, "end": v(757.84, 185.46) * mm});
            skLineSegment(sketch, "E935", {"start": v(757.84, 185.46) * mm, "end": v(759.22, 190.54) * mm});
            skLineSegment(sketch, "E936", {"start": v(759.22, 190.54) * mm, "end": v(765.93, 219.31) * mm});
            skLineSegment(sketch, "E937", {"start": v(765.93, 219.31) * mm, "end": v(766.96, 225.07) * mm});
            skLineSegment(sketch, "E938", {"start": v(766.96, 225.07) * mm, "end": v(767.72, 230.78) * mm});
            skLineSegment(sketch, "E939", {"start": v(767.72, 230.78) * mm, "end": v(768.14, 236.54) * mm});
            skLineSegment(sketch, "E940", {"start": v(768.14, 236.54) * mm, "end": v(768.14, 242.13) * mm});
            skLineSegment(sketch, "E941", {"start": v(768.14, 242.13) * mm, "end": v(767.64, 247.68) * mm});
            skLineSegment(sketch, "E942", {"start": v(767.64, 247.68) * mm, "end": v(766.52, 254.11) * mm});
            skLineSegment(sketch, "E943", {"start": v(766.52, 254.11) * mm, "end": v(765.01, 260.5) * mm});
            skLineSegment(sketch, "E944", {"start": v(765.01, 260.5) * mm, "end": v(763.2, 266.84) * mm});
            skLineSegment(sketch, "E945", {"start": v(763.2, 266.84) * mm, "end": v(761.14, 273.18) * mm});
            skLineSegment(sketch, "E946", {"start": v(761.14, 273.18) * mm, "end": v(752.16, 298.32) * mm});
            skLineSegment(sketch, "E947", {"start": v(752.16, 298.32) * mm, "end": v(750.14, 304.63) * mm});
            skLineSegment(sketch, "E948", {"start": v(750.14, 304.63) * mm, "end": v(748.36, 310.96) * mm});
            skLineSegment(sketch, "E949", {"start": v(748.36, 310.96) * mm, "end": v(746.95, 317.32) * mm});
            skLineSegment(sketch, "E950", {"start": v(746.95, 317.32) * mm, "end": v(745.94, 323.77) * mm});
            skLineSegment(sketch, "E951", {"start": v(745.94, 323.77) * mm, "end": v(735.73, 401.97) * mm});
            skLineSegment(sketch, "E952", {"start": v(735.73, 401.97) * mm, "end": v(723.82, 478.86) * mm});
            skLineSegment(sketch, "E953", {"start": v(723.82, 478.86) * mm, "end": v(710.82, 556.3) * mm});
            skLineSegment(sketch, "E954", {"start": v(710.82, 556.3) * mm, "end": v(696.2, 632.65) * mm});
            skLineSegment(sketch, "E955", {"start": v(696.2, 632.65) * mm, "end": v(680, 708.27) * mm});
            skLineSegment(sketch, "E956", {"start": v(680, 708.27) * mm, "end": v(662.28, 784.62) * mm});
            skLineSegment(sketch, "E957", {"start": v(662.28, 784.62) * mm, "end": v(642.97, 860) * mm});
            skLineSegment(sketch, "E958", {"start": v(642.97, 860) * mm, "end": v(622.13, 936.41) * mm});
            skLineSegment(sketch, "E959", {"start": v(622.13, 936.41) * mm, "end": v(600.09, 1011.4) * mm});
            skLineSegment(sketch, "E960", {"start": v(600.09, 1011.4) * mm, "end": v(571.58, 1101.47) * mm});
            skLineSegment(sketch, "E961", {"start": v(571.58, 1101.47) * mm, "end": v(526.48, 1236.55) * mm});
            skLineSegment(sketch, "E962", {"start": v(526.48, 1236.55) * mm, "end": v(523.7, 1244.61) * mm});
            skLineSegment(sketch, "E963", {"start": v(523.7, 1244.61) * mm, "end": v(520.58, 1252.46) * mm});
            skLineSegment(sketch, "E964", {"start": v(520.58, 1252.46) * mm, "end": v(517.17, 1259.82) * mm});
            skLineSegment(sketch, "E965", {"start": v(517.17, 1259.82) * mm, "end": v(513.15, 1266.8) * mm});
            skLineSegment(sketch, "E966", {"start": v(513.15, 1266.8) * mm, "end": v(508.51, 1273.24) * mm});
            skLineSegment(sketch, "E967", {"start": v(508.51, 1273.24) * mm, "end": v(503.12, 1278.99) * mm});
            skLineSegment(sketch, "E968", {"start": v(503.12, 1278.99) * mm, "end": v(496.77, 1283.96) * mm});
            skLineSegment(sketch, "E969", {"start": v(496.77, 1283.96) * mm, "end": v(489.38, 1288.09) * mm});
            skLineSegment(sketch, "E970", {"start": v(489.38, 1288.09) * mm, "end": v(480.87, 1291.2) * mm});
            skLineSegment(sketch, "E971", {"start": v(480.87, 1291.2) * mm, "end": v(471.08, 1293.24) * mm});
            skLineSegment(sketch, "E972", {"start": v(471.08, 1293.24) * mm, "end": v(466.44, 1294.59) * mm});
            skLineSegment(sketch, "E973", {"start": v(466.44, 1294.59) * mm, "end": v(461.86, 1297.1) * mm});
            skLineSegment(sketch, "E974", {"start": v(461.86, 1297.1) * mm, "end": v(457.49, 1300.49) * mm});
            skLineSegment(sketch, "E975", {"start": v(457.49, 1300.49) * mm, "end": v(453.14, 1304.59) * mm});
            skLineSegment(sketch, "E976", {"start": v(453.14, 1304.59) * mm, "end": v(449.01, 1309.41) * mm});
            skLineSegment(sketch, "E977", {"start": v(449.01, 1309.41) * mm, "end": v(445.3, 1314.35) * mm});
            skLineSegment(sketch, "E978", {"start": v(445.3, 1314.35) * mm, "end": v(441.95, 1319.43) * mm});
            skLineSegment(sketch, "E979", {"start": v(441.95, 1319.43) * mm, "end": v(439.1, 1324.39) * mm});
            skLineSegment(sketch, "E980", {"start": v(439.1, 1324.39) * mm, "end": v(430.28, 1341.71) * mm});
            skLineSegment(sketch, "E981", {"start": v(430.28, 1341.71) * mm, "end": v(417.83, 1368.14) * mm});
            skLineSegment(sketch, "E982", {"start": v(417.83, 1368.14) * mm, "end": v(397.37, 1412.34) * mm});
            skLineSegment(sketch, "E983", {"start": v(397.37, 1412.34) * mm, "end": v(388.69, 1429.61) * mm});
            skLineSegment(sketch, "E984", {"start": v(388.69, 1429.61) * mm, "end": v(384.1, 1438.17) * mm});
            skLineSegment(sketch, "E985", {"start": v(384.1, 1438.17) * mm, "end": v(379.4, 1446.58) * mm});
            skLineSegment(sketch, "E986", {"start": v(379.4, 1446.58) * mm, "end": v(374.4, 1454.87) * mm});
            skLineSegment(sketch, "E987", {"start": v(374.4, 1454.87) * mm, "end": v(353.57, 1487.46) * mm});
            skLineSegment(sketch, "E988", {"start": v(353.57, 1487.46) * mm, "end": v(338.72, 1512.2) * mm});
            skLineSegment(sketch, "E989", {"start": v(338.72, 1512.2) * mm, "end": v(324.53, 1537.32) * mm});
            skLineSegment(sketch, "E990", {"start": v(324.53, 1537.32) * mm, "end": v(311.02, 1562.68) * mm});
            skLineSegment(sketch, "E991", {"start": v(311.02, 1562.68) * mm, "end": v(298.2, 1588.31) * mm});
            skLineSegment(sketch, "E992", {"start": v(298.2, 1588.31) * mm, "end": v(286.02, 1614.28) * mm});
            skLineSegment(sketch, "E993", {"start": v(286.02, 1614.28) * mm, "end": v(274.33, 1640.5) * mm});
            skLineSegment(sketch, "E994", {"start": v(274.33, 1640.5) * mm, "end": v(263.32, 1667) * mm});
            skLineSegment(sketch, "E995", {"start": v(263.32, 1667) * mm, "end": v(252.78, 1693.68) * mm});
            skLineSegment(sketch, "E996", {"start": v(252.78, 1693.68) * mm, "end": v(242.78, 1720.66) * mm});
            skLineSegment(sketch, "E997", {"start": v(242.78, 1720.66) * mm, "end": v(228.6, 1761.52) * mm});
            skLineSegment(sketch, "E998", {"start": v(228.6, 1761.52) * mm, "end": v(220.13, 1787.19) * mm});
            skLineSegment(sketch, "E999", {"start": v(220.13, 1787.19) * mm, "end": v(211.57, 1810.82) * mm});
            skLineSegment(sketch, "E1000", {"start": v(211.57, 1810.82) * mm, "end": v(202.34, 1833.98) * mm});
            skLineSegment(sketch, "E1001", {"start": v(202.34, 1833.98) * mm, "end": v(197.47, 1845.29) * mm});
            skLineSegment(sketch, "E1002", {"start": v(197.47, 1845.29) * mm, "end": v(192.39, 1856.47) * mm});
            skLineSegment(sketch, "E1003", {"start": v(192.39, 1856.47) * mm, "end": v(187.05, 1867.65) * mm});
            skLineSegment(sketch, "E1004", {"start": v(187.05, 1867.65) * mm, "end": v(181.66, 1878.53) * mm});
            skLineSegment(sketch, "E1005", {"start": v(181.66, 1878.53) * mm, "end": v(176, 1889.32) * mm});
            skLineSegment(sketch, "E1006", {"start": v(176, 1889.32) * mm, "end": v(170.18, 1900) * mm});
            skLineSegment(sketch, "E1007", {"start": v(170.18, 1900) * mm, "end": v(164.22, 1910.47) * mm});
            skLineSegment(sketch, "E1008", {"start": v(164.22, 1910.47) * mm, "end": v(158.05, 1920.74) * mm});
            skLineSegment(sketch, "E1009", {"start": v(158.05, 1920.74) * mm, "end": v(151.72, 1930.84) * mm});
            skLineSegment(sketch, "E1010", {"start": v(151.72, 1930.84) * mm, "end": v(145.18, 1940.8) * mm});
            skLineSegment(sketch, "E1011", {"start": v(145.18, 1940.8) * mm, "end": v(138.49, 1950.55) * mm});
            skLineSegment(sketch, "E1012", {"start": v(138.49, 1950.55) * mm, "end": v(131.63, 1960.06) * mm});
            skLineSegment(sketch, "E1013", {"start": v(131.63, 1960.06) * mm, "end": v(124.6, 1969.39) * mm});
            skLineSegment(sketch, "E1014", {"start": v(124.6, 1969.39) * mm, "end": v(117.39, 1978.5) * mm});
            skLineSegment(sketch, "E1015", {"start": v(117.39, 1978.5) * mm, "end": v(101.59, 1961.05) * mm});
            skLineSegment(sketch, "E1016", {"start": v(101.59, 1961.05) * mm, "end": v(86.16, 1943.24) * mm});
            skLineSegment(sketch, "E1017", {"start": v(86.16, 1943.24) * mm, "end": v(71.21, 1925.38) * mm});
            skLineSegment(sketch, "E1018", {"start": v(71.21, 1925.38) * mm, "end": v(56.66, 1907.25) * mm});
            skLineSegment(sketch, "E1019", {"start": v(56.66, 1907.25) * mm, "end": v(28.58, 1870.5) * mm});
            skLineSegment(sketch, "E1020", {"start": v(28.58, 1870.5) * mm, "end": v(1.82, 1832.97) * mm});
            skLineSegment(sketch, "E1021", {"start": v(1.82, 1832.97) * mm, "end": v(-23.6, 1794.78) * mm});
            skLineSegment(sketch, "E1022", {"start": v(-23.6, 1794.78) * mm, "end": v(-47.81, 1755.99) * mm});
            skLineSegment(sketch, "E1023", {"start": v(-47.81, 1755.99) * mm, "end": v(-70.94, 1716.56) * mm});
            skLineSegment(sketch, "E1024", {"start": v(-70.94, 1716.56) * mm, "end": v(-93.04, 1676.63) * mm});
            skLineSegment(sketch, "E1025", {"start": v(-93.04, 1676.63) * mm, "end": v(-114.3, 1636.14) * mm});
            skLineSegment(sketch, "E1026", {"start": v(-114.3, 1636.14) * mm, "end": v(-134.7, 1595.2) * mm});
            skLineSegment(sketch, "E1027", {"start": v(-134.7, 1595.2) * mm, "end": v(-163.95, 1533.05) * mm});
            skLineSegment(sketch, "E1028", {"start": v(-163.95, 1533.05) * mm, "end": v(-192, 1470.14) * mm});
            skLineSegment(sketch, "E1029", {"start": v(-192, 1470.14) * mm, "end": v(-236.66, 1363.88) * mm});
            skLineSegment(sketch, "E1030", {"start": v(-236.66, 1363.88) * mm, "end": v(-297.5, 1213.62) * mm});
            skLineSegment(sketch, "E1031", {"start": v(-297.5, 1213.62) * mm, "end": v(-327.23, 1210.9) * mm});
            skLineSegment(sketch, "E1032", {"start": v(-327.23, 1210.9) * mm, "end": v(-326.3, 1196.42) * mm});
            skLineSegment(sketch, "E1033", {"start": v(-326.3, 1196.42) * mm, "end": v(-323.45, 1163.82) * mm});
            skLineSegment(sketch, "E1034", {"start": v(-323.45, 1163.82) * mm, "end": v(-323.13, 1157.73) * mm});
            skLineSegment(sketch, "E1035", {"start": v(-323.13, 1157.73) * mm, "end": v(-323, 1151.78) * mm});
            skLineSegment(sketch, "E1036", {"start": v(-323, 1151.78) * mm, "end": v(-323.1, 1145.95) * mm});
            skLineSegment(sketch, "E1037", {"start": v(-323.1, 1145.95) * mm, "end": v(-323.46, 1140.21) * mm});
            skLineSegment(sketch, "E1038", {"start": v(-323.46, 1140.21) * mm, "end": v(-324.11, 1134.5) * mm});
            skLineSegment(sketch, "E1039", {"start": v(-324.11, 1134.5) * mm, "end": v(-357.87, 905.19) * mm});
            skLineSegment(sketch, "E1040", {"start": v(-357.87, 905.19) * mm, "end": v(-369.41, 838.05) * mm});
            skLineSegment(sketch, "E1041", {"start": v(-369.41, 838.05) * mm, "end": v(-379.76, 784.54) * mm});
            skLineSegment(sketch, "E1042", {"start": v(-379.76, 784.54) * mm, "end": v(-395.52, 712.21) * mm});
            skLineSegment(sketch, "E1043", {"start": v(-395.52, 712.21) * mm, "end": v(-419.48, 611.6) * mm});
            skLineSegment(sketch, "E1044", {"start": v(-419.48, 611.6) * mm, "end": v(-478.64, 377.33) * mm});
            skLineSegment(sketch, "E1045", {"start": v(-478.64, 377.33) * mm, "end": v(-491.92, 319.68) * mm});
            skLineSegment(sketch, "E1046", {"start": v(-491.92, 319.68) * mm, "end": v(-496.81, 300.55) * mm});
            skLineSegment(sketch, "E1047", {"start": v(-496.81, 300.55) * mm, "end": v(-499.48, 291.11) * mm});
            skLineSegment(sketch, "E1048", {"start": v(-499.48, 291.11) * mm, "end": v(-502.32, 281.71) * mm});
            skLineSegment(sketch, "E1049", {"start": v(-502.32, 281.71) * mm, "end": v(-505.42, 272.44) * mm});
            skLineSegment(sketch, "E1050", {"start": v(-505.42, 272.44) * mm, "end": v(-508.7, 263.34) * mm});
            skLineSegment(sketch, "E1051", {"start": v(-508.7, 263.34) * mm, "end": v(-512.26, 254.26) * mm});
            skLineSegment(sketch, "E1052", {"start": v(-512.26, 254.26) * mm, "end": v(-516.06, 245.42) * mm});
            skLineSegment(sketch, "E1053", {"start": v(-516.06, 245.42) * mm, "end": v(-520.2, 236.69) * mm});
            skLineSegment(sketch, "E1054", {"start": v(-520.2, 236.69) * mm, "end": v(-532.84, 210.91) * mm});
            skLineSegment(sketch, "E1055", {"start": v(-532.84, 210.91) * mm, "end": v(-536.61, 202.63) * mm});
            skLineSegment(sketch, "E1056", {"start": v(-536.61, 202.63) * mm, "end": v(-539.98, 194.42) * mm});
            skLineSegment(sketch, "E1057", {"start": v(-539.98, 194.42) * mm, "end": v(-542.9, 186.23) * mm});
            skLineSegment(sketch, "E1058", {"start": v(-542.9, 186.23) * mm, "end": v(-545.25, 178.11) * mm});
            skLineSegment(sketch, "E1059", {"start": v(-545.25, 178.11) * mm, "end": v(-546.97, 170) * mm});
            skLineSegment(sketch, "E1060", {"start": v(-546.97, 170) * mm, "end": v(-547.96, 161.9) * mm});
            skLineSegment(sketch, "E1061", {"start": v(-547.96, 161.9) * mm, "end": v(-548.14, 153.76) * mm});
            skLineSegment(sketch, "E1062", {"start": v(-548.14, 153.76) * mm, "end": v(-547.42, 145.51) * mm});
            skLineSegment(sketch, "E1063", {"start": v(-547.42, 145.51) * mm, "end": v(-545.72, 137.26) * mm});
            skLineSegment(sketch, "E1064", {"start": v(-545.72, 137.26) * mm, "end": v(-542.94, 128.88) * mm});
            skLineSegment(sketch, "E1065", {"start": v(-542.94, 128.88) * mm, "end": v(-539, 120.38) * mm});
            skLineSegment(sketch, "E1066", {"start": v(-539, 120.38) * mm, "end": v(-533.8, 111.7) * mm});
            skLineSegment(sketch, "E1067", {"start": v(-533.8, 111.7) * mm, "end": v(-527.3, 102.9) * mm});
            skLineSegment(sketch, "E1068", {"start": v(-527.3, 102.9) * mm, "end": v(-525.75, 100.11) * mm});
            skLineSegment(sketch, "E1069", {"start": v(-525.75, 100.11) * mm, "end": v(-524.91, 96.74) * mm});
            skLineSegment(sketch, "E1070", {"start": v(-524.91, 96.74) * mm, "end": v(-524.61, 93.03) * mm});
            skLineSegment(sketch, "E1071", {"start": v(-524.61, 93.03) * mm, "end": v(-524.66, 88.94) * mm});
            skLineSegment(sketch, "E1072", {"start": v(-524.66, 88.94) * mm, "end": v(-525, 80.61) * mm});
            skLineSegment(sketch, "E1073", {"start": v(-525, 80.61) * mm, "end": v(-524.91, 76.7) * mm});
            skLineSegment(sketch, "E1074", {"start": v(-524.91, 76.7) * mm, "end": v(-503.47, -232.52) * mm});
            skSolve(sketch);
        }
        {
            var Q0;
            Q0=makeQuery(id+"F0.imprint","IMPRINT",FACE,{"disambiguationData":[TD([[makeQuery(id+"F0.imprint","IMPRINT",EDGE,{"derivedFrom":sQuery(id+"F0.wireOp",EDGE,"E0")}),1.0]])]});
            extrude(context, id + "F1", {"entities" : qUnion([Q0]), "endBound" : BoundingType.SYMMETRIC, "depth" : 254 * mm, "offsetDistance" : 25.4 * mm});
        }
    });
